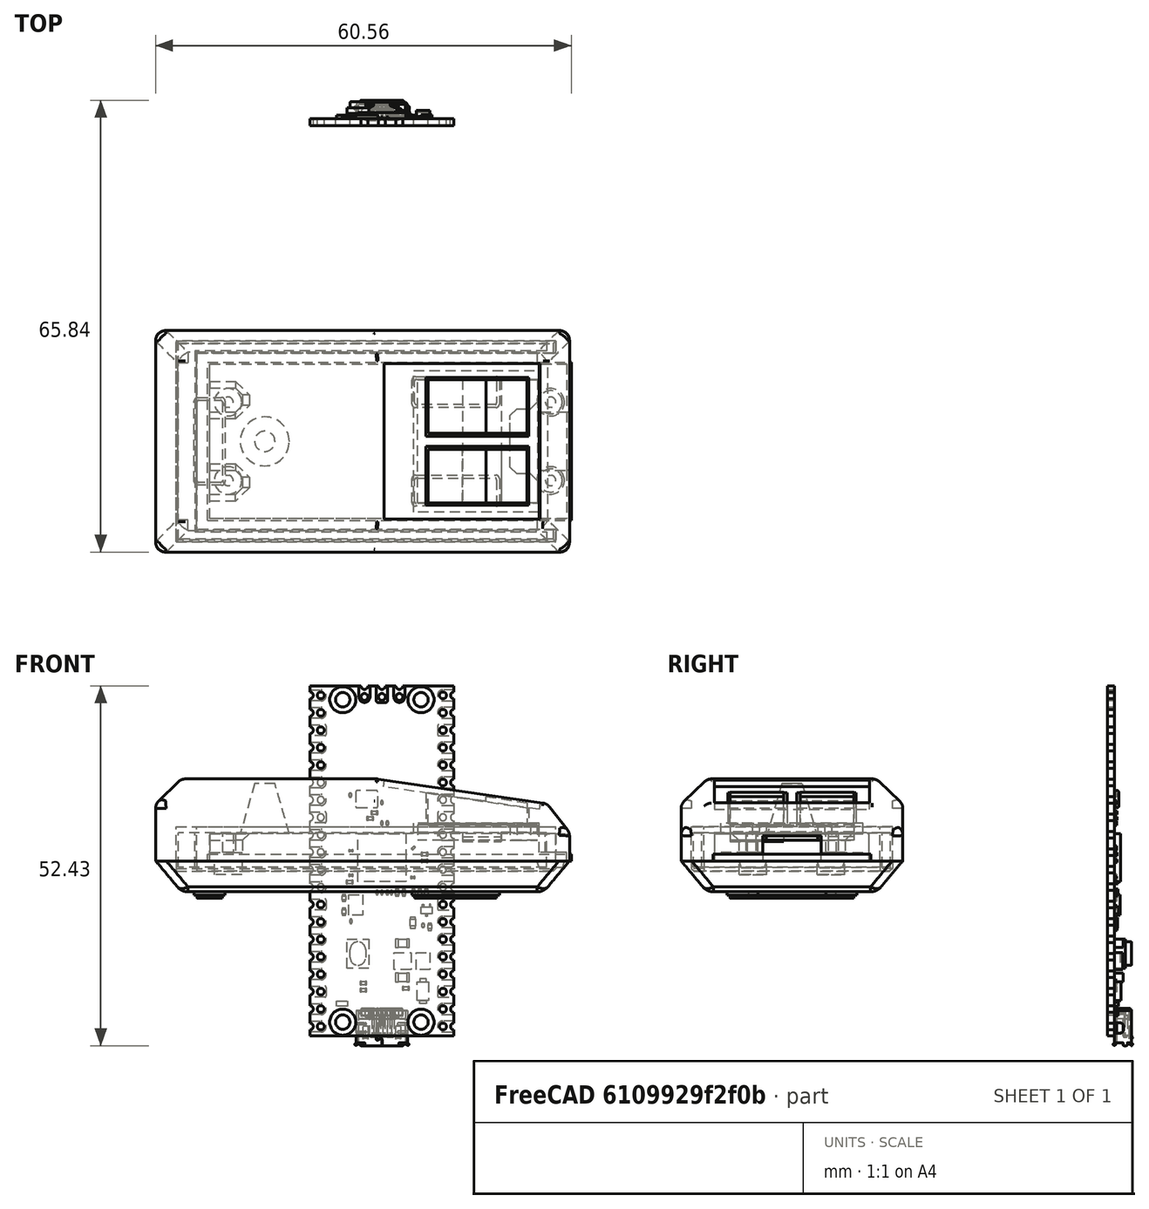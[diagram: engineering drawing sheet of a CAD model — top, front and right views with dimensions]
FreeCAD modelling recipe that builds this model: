
FCSTD DOCUMENT  (FreeCAD 0.22R36731 (Git))
Label: mouse
License: All rights reserved
LicenseURL: http://en.wikipedia.org/wiki/All_rights_reserved
objects: Part::Feature×116, App::Part×35, Sketcher::SketchObject×27, PartDesign::Pad×16, PartDesign::Pocket×16, PartDesign::Body×6, PartDesign::Chamfer×3, PartDesign::Fillet×2, Mesh::Feature×1, PartDesign::Plane×1, Part::Box×1
note: 225 computed .brp shape members not serialized (recipe doc carries the construction recipe); baked Part::Feature solids carry a one-line shape summary decoded from their .brp

FEATURE [Sketcher::SketchObject] Sketch
  AttachmentSupport = -> [XZ_Plane]
  FullyConstrained = true
  MapMode = 5
  Placement = pos=(0,0,0) rot=(1,0,0;1.5708rad)
  sketch-geometry (14):
    g0: LineSegment StartX=21.1514 StartY=8.48067 StartZ=0 EndX=15.1514 EndY=9.36067 EndZ=0
    g1: LineSegment StartX=15.1514 StartY=9.36067 StartZ=0 EndX=15.1514 EndY=8.76067 EndZ=0
    g2: LineSegment StartX=15.1514 StartY=8.76067 StartZ=0 EndX=6.70138 EndY=10 EndZ=0
    g3: LineSegment StartX=6.70138 StartY=10 StartZ=0 EndX=6.70138 EndY=5.25 EndZ=0
    g4: LineSegment StartX=6.70138 StartY=5.25 StartZ=0 EndX=5.20138 EndY=5.25 EndZ=0
    g5: LineSegment StartX=5.20138 StartY=5.25 StartZ=0 EndX=5.20138 EndY=4.25 EndZ=0
    g6: LineSegment StartX=5.20138 StartY=4.25 StartZ=0 EndX=11.74 EndY=4.25 EndZ=0
    g7: LineSegment StartX=11.74 StartY=4.25 StartZ=0 EndX=11.74 EndY=3 EndZ=0
    g8: LineSegment StartX=11.74 StartY=3 StartZ=0 EndX=17.37 EndY=3 EndZ=0
    g9: LineSegment StartX=17.37 StartY=3 StartZ=0 EndX=17.37 EndY=4.25 EndZ=0
    g10: LineSegment StartX=17.37 StartY=4.25 StartZ=0 EndX=22.6514 EndY=4.25 EndZ=0
    g11: LineSegment StartX=22.6514 StartY=4.25 StartZ=0 EndX=22.6514 EndY=5.25 EndZ=0
    g12: LineSegment StartX=22.6514 StartY=5.25 StartZ=0 EndX=21.1514 EndY=5.25 EndZ=0
    g13: LineSegment StartX=21.1514 StartY=5.25 StartZ=0 EndX=21.1514 EndY=8.48067 EndZ=0
  constraints (42):
    c: Coincident(g0,g1)
    c: Vertical(g1)
    c: Coincident(g1,g2)
    c: Coincident(g2,g3)
    c: Vertical(g3)
    c: Coincident(g3,g4)
    c: Coincident(g4,g5)
    c: Vertical(g5)
    c: Coincident(g5,g6)
    c: Horizontal(g6)
    c: Coincident(g6,g7)
    c: Coincident(g7,g8)
    c: Horizontal(g8)
    c: Coincident(g8,g9)
    c: Coincident(g9,g10)
    c: Coincident(g10,g11)
    c: Vertical(g11)
    c: Coincident(g11,g12)
    c: Coincident(g12,g13)
    c: Coincident(g13,g0)
    c: Vertical(g13)
    c: Parallel(g0,g2)
    c: DistanceX(g0) = 21.1514
    c: DistanceX(g0,g0) = 6
    c: DistanceX(g2,g2) = 8.45
    c: DistanceY(g0,g0) = 0.88
    c: DistanceY(g1,g1) = 0.6
    c: Vertical(g9)
    c: Vertical(g7)
    c: Horizontal(g10)
    c: Equal(g7,g9)
    c: DistanceX(g7) = 11.74
    c: DistanceX(g8,g8) = 5.63
    c: DistanceX(g4,g3) = 1.5
    c: DistanceY(g7) = 3
    c: Horizontal(g12)
    c: DistanceX(g12,g12) = 1.5
    c: Horizontal(g4)
    c: PointOnObject(g3,g12)
    c: DistanceY(g5,g5) = 1
    c: DistanceY(g7,g7) = 1.25
    c: DistanceY(g3,g3) = 4.75
FEATURE [PartDesign::Pad] Pad
  Direction = (0,-1,2e-16)
  Length = 18
  Length2 = 10
  Placement = pos=(0,0,0) rot=(1,0,0;1.5708rad)
  Profile = -> Sketch
  ReferenceAxis = -> Sketch [N_Axis]
  Refine = true
  Suppressed = false
  Type = 0
FEATURE [Mesh::Feature] mouse_bottom
FEATURE [Part::Feature] Part__Feature  label="PCB, Raspberry Pi Pico-R3"
  shape: bbox 21 x 1 x 51 mm, 416 faces (baked)
FEATURE [Part::Feature] Part__Feature001  label="MicroUSB Port, Raspberry Pi Pico-R3"
  Placement = pos=(0,0.5,-24.35) rot=(0,1,0;3.14159rad)
  shape: bbox 7.999 x 2.949 x 5.461 mm, 809 faces (baked)
FEATURE [Part::Feature] Part__Feature002  label="MicroUSB Port, Raspberry Pi Pico-R004"
  Placement = pos=(0,0.5,-24.35) rot=(0,1,0;3.14159rad)
  shape: bbox 6.982 x 2.155 x 3.937 mm, 206 faces (baked)
FEATURE [Part::Feature] Part__Feature003  label="MicroUSB Port, Raspberry Pi Pico-R005"
  Placement = pos=(0,0.5,-24.35) rot=(0,1,0;3.14159rad)
  shape: bbox 0.37 x 1.716 x 4 mm, 43 faces (baked)
FEATURE [Part::Feature] Part__Feature004  label="MicroUSB Port, Raspberry Pi Pico-R006"
  Placement = pos=(0,0.5,-24.35) rot=(0,1,0;3.14159rad)
  shape: bbox 0.37 x 1.716 x 4 mm, 43 faces (baked)
FEATURE [Part::Feature] Part__Feature005  label="MicroUSB Port, Raspberry Pi Pico-R007"
  Placement = pos=(0,0.5,-24.35) rot=(0,1,0;3.14159rad)
  shape: bbox 0.37 x 1.716 x 4 mm, 43 faces (baked)
FEATURE [Part::Feature] Part__Feature006  label="MicroUSB Port, Raspberry Pi Pico-R008"
  Placement = pos=(0,0.5,-24.35) rot=(0,1,0;3.14159rad)
  shape: bbox 0.37 x 1.716 x 4 mm, 43 faces (baked)
FEATURE [Part::Feature] Part__Feature007  label="MicroUSB Port, Raspberry Pi Pico-R009"
  Placement = pos=(0,0.5,-24.35) rot=(0,1,0;3.14159rad)
  shape: bbox 0.37 x 1.716 x 4 mm, 43 faces (baked)
FEATURE [App::Part] MicroUSB_Port__Raspberry_Pi_Pico_R3  label="MicroUSB Port, Raspberry Pi Pico-R010"
  Group = -> [Part__Feature001,Part__Feature002,Part__Feature003,Part__Feature004,Part__Feature005,Part__Feature006,Part__Feature007]
  Origin = -> Origin001
FEATURE [Part::Feature] Part__Feature008  label="RP2040 Microcontroller, Raspberry Pi Pico-R3"
  Placement = pos=(0,0.5,0.5) rot=(0,0,1;0rad)
  shape: bbox 7 x 0.9 x 7 mm, 6 faces (baked)
FEATURE [Part::Feature] Part__Feature009  label="SW1, Tact Switch, Raspberry Pi Pico-R3"
  Placement = pos=(-3.5,0.5,-13.5) rot=(0,0,1;0rad)
  shape: bbox 3.2 x 2.5 x 4.25 mm, 17 faces (baked)
FEATURE [Part::Feature] Part__Feature010  label="D1, Diode, Schottky, Raspberry Pi Pico-R3"
  Placement = pos=(6,0.5,-19) rot=(0,0,1;0rad)
  shape: bbox 1.65 x 0.95 x 3.6 mm, 14 faces (baked)
FEATURE [Part::Feature] Part__Feature011  label="D2, QSME-C194, LED, Raspberry Pi Pico-R3"
  Placement = pos=(-5.8,0.5,-20.8) rot=(0,0,1;0rad)
  shape: bbox 1.6 x 0.55 x 0.8 mm, 6 faces (baked)
FEATURE [Part::Feature] Part__Feature012  label="L1, Inductor, Raspberry Pi Pico-R3"
  Placement = pos=(6,0.5,-14.6) rot=(0,0,1;0rad)
  shape: bbox 2 x 1.2 x 2.5 mm, 6 faces (baked)
FEATURE [Part::Feature] Part__Feature013  label="U2, RT6150B-33GQW, Buck Boost Converter, Raspberry Pi Pico-R3"
  Placement = pos=(3,0.5,-14.6) rot=(0,0,1;0rad)
  shape: bbox 2.5 x 0.8 x 2.5 mm, 6 faces (baked)
FEATURE [Part::Feature] Part__Feature014  label="U3, W25Q16JVUXIQ, Serial NOR Flash 16 Mbit, Raspberry Pi Pico-R3"
  Placement = pos=(-3.8,0.5,-6.4) rot=(0,0,1;0rad)
  shape: bbox 2 x 0.8 x 3 mm, 6 faces (baked)
FEATURE [Part::Feature] Part__Feature015  label="Q1, MOSFET, DMG1012T, Raspberry Pi Pico-R3"
  Placement = pos=(6.5,0.5,-7.2) rot=(0,0,1;0rad)
  shape: bbox 1.6 x 0.6 x 1.8 mm, 18 faces (baked)
FEATURE [Part::Feature] Part__Feature016  label="X1, X12M000000S096, 12 Mhz Crystal Resonator, Raspberry Pi Pico-R3"
  Placement = pos=(-2.2,0.5,9) rot=(0,0,1;0rad)
  shape: bbox 3.2 x 0.6 x 2.5 mm, 18 faces (baked)
FEATURE [Part::Feature] Part__Feature017  label="SMD Resistor, Configurable, Raspberry Pi Pico-R3_R1"
  Placement = pos=(6.2,0.5,1) rot=(0,1,0;1.5708rad)
  shape: bbox 0.6 x 0.35 x 0.5 mm, 6 faces (baked)
FEATURE [Part::Feature] Part__Feature018  label="SMD Resistor, Configurable, Raspberry Pi Pico-R3_R002"
  Placement = pos=(6.2,0.5,1) rot=(0,1,0;1.5708rad)
  shape: bbox 0.2 x 0.35 x 0.5 mm, 6 faces (baked)
FEATURE [Part::Feature] Part__Feature019  label="SMD Resistor, Configurable, Raspberry Pi Pico-R3_R003"
  Placement = pos=(6.2,0.5,1) rot=(0,1,0;1.5708rad)
  shape: bbox 0.2 x 0.35 x 0.5 mm, 6 faces (baked)
FEATURE [App::Part] SMD_Resistor__Configurable__Raspberry_Pi_Pico_R3_R1  label="SMD Resistor, Configurable, Raspberry Pi Pico-R3_R004"
  Group = -> [Part__Feature017,Part__Feature018,Part__Feature019]
  Origin = -> Origin002
FEATURE [Part::Feature] Part__Feature020  label="SMD Resistor, Configurable, Raspberry Pi Pico-R3_R2"
  Placement = pos=(3.5,0.5,-18.6) rot=(0,1,0;1.5708rad)
  shape: bbox 0.6 x 0.35 x 0.5 mm, 6 faces (baked)
FEATURE [Part::Feature] Part__Feature021  label="SMD Resistor, Configurable, Raspberry Pi Pico-R3_R005"
  Placement = pos=(3.5,0.5,-18.6) rot=(0,1,0;1.5708rad)
  shape: bbox 0.2 x 0.35 x 0.5 mm, 6 faces (baked)
FEATURE [Part::Feature] Part__Feature022  label="SMD Resistor, Configurable, Raspberry Pi Pico-R3_R006"
  Placement = pos=(3.5,0.5,-18.6) rot=(0,1,0;1.5708rad)
  shape: bbox 0.2 x 0.35 x 0.5 mm, 6 faces (baked)
FEATURE [App::Part] SMD_Resistor__Configurable__Raspberry_Pi_Pico_R3_R2  label="SMD Resistor, Configurable, Raspberry Pi Pico-R3_R007"
  Group = -> [Part__Feature020,Part__Feature021,Part__Feature022]
  Origin = -> Origin003
FEATURE [Part::Feature] Part__Feature023  label="SMD Resistor, Configurable, Raspberry Pi Pico-R3_R3"
  Placement = pos=(-2.7,0.5,-17.8) rot=(0,1,0;1.5708rad)
  shape: bbox 0.6 x 0.35 x 0.5 mm, 6 faces (baked)
FEATURE [Part::Feature] Part__Feature024  label="SMD Resistor, Configurable, Raspberry Pi Pico-R3_R008"
  Placement = pos=(-2.7,0.5,-17.8) rot=(0,1,0;1.5708rad)
  shape: bbox 0.2 x 0.35 x 0.5 mm, 6 faces (baked)
FEATURE [Part::Feature] Part__Feature025  label="SMD Resistor, Configurable, Raspberry Pi Pico-R3_R009"
  Placement = pos=(-2.7,0.5,-17.8) rot=(0,1,0;1.5708rad)
  shape: bbox 0.2 x 0.35 x 0.5 mm, 6 faces (baked)
FEATURE [App::Part] SMD_Resistor__Configurable__Raspberry_Pi_Pico_R3_R3  label="SMD Resistor, Configurable, Raspberry Pi Pico-R3_R010"
  Group = -> [Part__Feature023,Part__Feature024,Part__Feature025]
  Origin = -> Origin004
FEATURE [Part::Feature] Part__Feature026  label="SMD Resistor, Configurable, Raspberry Pi Pico-R3_R4"
  Placement = pos=(-5.5,0.5,-5.4) rot=(0,1,0;3.14159rad)
  shape: bbox 0.5 x 0.35 x 0.6 mm, 6 faces (baked)
FEATURE [Part::Feature] Part__Feature027  label="SMD Resistor, Configurable, Raspberry Pi Pico-R3_R011"
  Placement = pos=(-5.5,0.5,-5.4) rot=(0,1,0;3.14159rad)
  shape: bbox 0.5 x 0.35 x 0.2 mm, 6 faces (baked)
FEATURE [Part::Feature] Part__Feature028  label="SMD Resistor, Configurable, Raspberry Pi Pico-R3_R012"
  Placement = pos=(-5.5,0.5,-5.4) rot=(0,1,0;3.14159rad)
  shape: bbox 0.5 x 0.35 x 0.2 mm, 6 faces (baked)
FEATURE [App::Part] SMD_Resistor__Configurable__Raspberry_Pi_Pico_R3_R4  label="SMD Resistor, Configurable, Raspberry Pi Pico-R3_R013"
  Group = -> [Part__Feature026,Part__Feature027,Part__Feature028]
  Origin = -> Origin005
FEATURE [Part::Feature] Part__Feature029  label="SMD Resistor, Configurable, Raspberry Pi Pico-R3_R5"
  Placement = pos=(7,0.5,-9.6) rot=(0,1,0;3.14159rad)
  shape: bbox 0.5 x 0.35 x 0.6 mm, 6 faces (baked)
FEATURE [Part::Feature] Part__Feature030  label="SMD Resistor, Configurable, Raspberry Pi Pico-R3_R014"
  Placement = pos=(7,0.5,-9.6) rot=(0,1,0;3.14159rad)
  shape: bbox 0.5 x 0.35 x 0.2 mm, 6 faces (baked)
FEATURE [Part::Feature] Part__Feature031  label="SMD Resistor, Configurable, Raspberry Pi Pico-R3_R015"
  Placement = pos=(7,0.5,-9.6) rot=(0,1,0;3.14159rad)
  shape: bbox 0.5 x 0.35 x 0.2 mm, 6 faces (baked)
FEATURE [App::Part] SMD_Resistor__Configurable__Raspberry_Pi_Pico_R3_R5  label="SMD Resistor, Configurable, Raspberry Pi Pico-R3_R016"
  Group = -> [Part__Feature029,Part__Feature030,Part__Feature031]
  Origin = -> Origin006
FEATURE [Part::Feature] Part__Feature032  label="SMD Resistor, Configurable, Raspberry Pi Pico-R3_R6"
  Placement = pos=(6.5,0.5,-4.6) rot=(0,1,0;3.14159rad)
  shape: bbox 0.5 x 0.35 x 0.6 mm, 6 faces (baked)
FEATURE [Part::Feature] Part__Feature033  label="SMD Resistor, Configurable, Raspberry Pi Pico-R3_R017"
  Placement = pos=(6.5,0.5,-4.6) rot=(0,1,0;3.14159rad)
  shape: bbox 0.5 x 0.35 x 0.2 mm, 6 faces (baked)
FEATURE [Part::Feature] Part__Feature034  label="SMD Resistor, Configurable, Raspberry Pi Pico-R3_R018"
  Placement = pos=(6.5,0.5,-4.6) rot=(0,1,0;3.14159rad)
  shape: bbox 0.5 x 0.35 x 0.2 mm, 6 faces (baked)
FEATURE [App::Part] SMD_Resistor__Configurable__Raspberry_Pi_Pico_R3_R6  label="SMD Resistor, Configurable, Raspberry Pi Pico-R3_R019"
  Group = -> [Part__Feature032,Part__Feature033,Part__Feature034]
  Origin = -> Origin007
FEATURE [Part::Feature] Part__Feature035  label="SMD Resistor, Configurable, Raspberry Pi Pico-R3_R7"
  Placement = pos=(4.5,0.5,-9) rot=(0,1,0;3.14159rad)
  shape: bbox 0.8 x 0.45 x 1 mm, 6 faces (baked)
FEATURE [Part::Feature] Part__Feature036  label="SMD Resistor, Configurable, Raspberry Pi Pico-R3_R020"
  Placement = pos=(4.5,0.5,-9) rot=(0,1,0;3.14159rad)
  shape: bbox 0.8 x 0.45 x 0.3 mm, 6 faces (baked)
FEATURE [Part::Feature] Part__Feature037  label="SMD Resistor, Configurable, Raspberry Pi Pico-R3_R021"
  Placement = pos=(4.5,0.5,-9) rot=(0,1,0;3.14159rad)
  shape: bbox 0.8 x 0.45 x 0.3 mm, 6 faces (baked)
FEATURE [App::Part] SMD_Resistor__Configurable__Raspberry_Pi_Pico_R3_R7  label="SMD Resistor, Configurable, Raspberry Pi Pico-R3_R022"
  Group = -> [Part__Feature035,Part__Feature036,Part__Feature037]
  Origin = -> Origin008
FEATURE [Part::Feature] Part__Feature038  label="SMD Resistor, Configurable, Raspberry Pi Pico-R3_R8"
  Placement = pos=(-2.7,0.5,-18.8) rot=(0,1,0;1.5708rad)
  shape: bbox 0.6 x 0.35 x 0.5 mm, 6 faces (baked)
FEATURE [Part::Feature] Part__Feature039  label="SMD Resistor, Configurable, Raspberry Pi Pico-R3_R023"
  Placement = pos=(-2.7,0.5,-18.8) rot=(0,1,0;1.5708rad)
  shape: bbox 0.2 x 0.35 x 0.5 mm, 6 faces (baked)
FEATURE [Part::Feature] Part__Feature040  label="SMD Resistor, Configurable, Raspberry Pi Pico-R3_R024"
  Placement = pos=(-2.7,0.5,-18.8) rot=(0,1,0;1.5708rad)
  shape: bbox 0.2 x 0.35 x 0.5 mm, 6 faces (baked)
FEATURE [App::Part] SMD_Resistor__Configurable__Raspberry_Pi_Pico_R3_R8  label="SMD Resistor, Configurable, Raspberry Pi Pico-R3_R025"
  Group = -> [Part__Feature038,Part__Feature039,Part__Feature040]
  Origin = -> Origin009
FEATURE [Part::Feature] Part__Feature041  label="SMD Resistor, Configurable, Raspberry Pi Pico-R3_R9"
  Placement = pos=(5.5,0.5,-4.6) rot=(0,1,0;3.14159rad)
  shape: bbox 0.5 x 0.35 x 0.6 mm, 6 faces (baked)
FEATURE [Part::Feature] Part__Feature042  label="SMD Resistor, Configurable, Raspberry Pi Pico-R3_R026"
  Placement = pos=(5.5,0.5,-4.6) rot=(0,1,0;3.14159rad)
  shape: bbox 0.5 x 0.35 x 0.2 mm, 6 faces (baked)
FEATURE [Part::Feature] Part__Feature043  label="SMD Resistor, Configurable, Raspberry Pi Pico-R3_R027"
  Placement = pos=(5.5,0.5,-4.6) rot=(0,1,0;3.14159rad)
  shape: bbox 0.5 x 0.35 x 0.2 mm, 6 faces (baked)
FEATURE [App::Part] SMD_Resistor__Configurable__Raspberry_Pi_Pico_R3_R9  label="SMD Resistor, Configurable, Raspberry Pi Pico-R3_R028"
  Group = -> [Part__Feature041,Part__Feature042,Part__Feature043]
  Origin = -> Origin010
FEATURE [Part::Feature] Part__Feature044  label="SMD Resistor, Configurable, Raspberry Pi Pico-R3_R10"
  Placement = pos=(6.2,0.5,-1e-16) rot=(0,1,0;1.5708rad)
  shape: bbox 0.6 x 0.35 x 0.5 mm, 6 faces (baked)
FEATURE [Part::Feature] Part__Feature045  label="SMD Resistor, Configurable, Raspberry Pi Pico-R3_R029"
  Placement = pos=(6.2,0.5,-1e-16) rot=(0,1,0;1.5708rad)
  shape: bbox 0.2 x 0.35 x 0.5 mm, 6 faces (baked)
FEATURE [Part::Feature] Part__Feature046  label="SMD Resistor, Configurable, Raspberry Pi Pico-R3_R030"
  Placement = pos=(6.2,0.5,-1e-16) rot=(0,1,0;1.5708rad)
  shape: bbox 0.2 x 0.35 x 0.5 mm, 6 faces (baked)
FEATURE [App::Part] SMD_Resistor__Configurable__Raspberry_Pi_Pico_R3_R10  label="SMD Resistor, Configurable, Raspberry Pi Pico-R3_R031"
  Group = -> [Part__Feature044,Part__Feature045,Part__Feature046]
  Origin = -> Origin011
FEATURE [Part::Feature] Part__Feature047  label="SMD Resistor, Configurable, Raspberry Pi Pico-R3_R11"
  Placement = pos=(-5.5,0.5,-7.4) rot=(0,0,1;0rad)
  shape: bbox 0.5 x 0.35 x 0.6 mm, 6 faces (baked)
FEATURE [Part::Feature] Part__Feature048  label="SMD Resistor, Configurable, Raspberry Pi Pico-R3_R032"
  Placement = pos=(-5.5,0.5,-7.4) rot=(0,0,1;0rad)
  shape: bbox 0.5 x 0.35 x 0.2 mm, 6 faces (baked)
FEATURE [Part::Feature] Part__Feature049  label="SMD Resistor, Configurable, Raspberry Pi Pico-R3_R033"
  Placement = pos=(-5.5,0.5,-7.4) rot=(0,0,1;0rad)
  shape: bbox 0.5 x 0.35 x 0.2 mm, 6 faces (baked)
FEATURE [App::Part] SMD_Resistor__Configurable__Raspberry_Pi_Pico_R3_R11  label="SMD Resistor, Configurable, Raspberry Pi Pico-R3_R034"
  Group = -> [Part__Feature047,Part__Feature048,Part__Feature049]
  Origin = -> Origin012
FEATURE [Part::Feature] Part__Feature050  label="SMD Resistor, Configurable, Raspberry Pi Pico-R3_R12"
  Placement = pos=(0.8,0.5,-4.6) rot=(0,1,0;3.14159rad)
  shape: bbox 0.3 x 0.23 x 0.4 mm, 6 faces (baked)
FEATURE [Part::Feature] Part__Feature051  label="SMD Resistor, Configurable, Raspberry Pi Pico-R3_R035"
  Placement = pos=(0.8,0.5,-4.6) rot=(0,1,0;3.14159rad)
  shape: bbox 0.3 x 0.23 x 0.1 mm, 6 faces (baked)
FEATURE [Part::Feature] Part__Feature052  label="SMD Resistor, Configurable, Raspberry Pi Pico-R3_R036"
  Placement = pos=(0.8,0.5,-4.6) rot=(0,1,0;3.14159rad)
  shape: bbox 0.3 x 0.23 x 0.1 mm, 6 faces (baked)
FEATURE [App::Part] SMD_Resistor__Configurable__Raspberry_Pi_Pico_R3_R12  label="SMD Resistor, Configurable, Raspberry Pi Pico-R3_R037"
  Group = -> [Part__Feature050,Part__Feature051,Part__Feature052]
  Origin = -> Origin013
FEATURE [Part::Feature] Part__Feature053  label="SMD Resistor, Configurable, Raspberry Pi Pico-R3_R13"
  Placement = pos=(1.4,0.5,-4.6) rot=(0,1,0;3.14159rad)
  shape: bbox 0.3 x 0.23 x 0.4 mm, 6 faces (baked)
FEATURE [Part::Feature] Part__Feature054  label="SMD Resistor, Configurable, Raspberry Pi Pico-R3_R038"
  Placement = pos=(1.4,0.5,-4.6) rot=(0,1,0;3.14159rad)
  shape: bbox 0.3 x 0.23 x 0.1 mm, 6 faces (baked)
FEATURE [Part::Feature] Part__Feature055  label="SMD Resistor, Configurable, Raspberry Pi Pico-R3_R039"
  Placement = pos=(1.4,0.5,-4.6) rot=(0,1,0;3.14159rad)
  shape: bbox 0.3 x 0.23 x 0.1 mm, 6 faces (baked)
FEATURE [App::Part] SMD_Resistor__Configurable__Raspberry_Pi_Pico_R3_R13  label="SMD Resistor, Configurable, Raspberry Pi Pico-R3_R040"
  Group = -> [Part__Feature053,Part__Feature054,Part__Feature055]
  Origin = -> Origin014
FEATURE [Part::Feature] Part__Feature056  label="SMD Resistor, Configurable, Raspberry Pi Pico-R3_R14"
  Placement = pos=(-1.1,0.5,7) rot=(0,1,0;1.5708rad)
  shape: bbox 0.6 x 0.35 x 0.5 mm, 6 faces (baked)
FEATURE [Part::Feature] Part__Feature057  label="SMD Resistor, Configurable, Raspberry Pi Pico-R3_R041"
  Placement = pos=(-1.1,0.5,7) rot=(0,1,0;1.5708rad)
  shape: bbox 0.2 x 0.35 x 0.5 mm, 6 faces (baked)
FEATURE [Part::Feature] Part__Feature058  label="SMD Resistor, Configurable, Raspberry Pi Pico-R3_R042"
  Placement = pos=(-1.1,0.5,7) rot=(0,1,0;1.5708rad)
  shape: bbox 0.2 x 0.35 x 0.5 mm, 6 faces (baked)
FEATURE [App::Part] SMD_Resistor__Configurable__Raspberry_Pi_Pico_R3_R14  label="SMD Resistor, Configurable, Raspberry Pi Pico-R3_R043"
  Group = -> [Part__Feature056,Part__Feature057,Part__Feature058]
  Origin = -> Origin015
FEATURE [Part::Feature] Part__Feature059  label="SMD Resistor, Configurable, Raspberry Pi Pico-R3_R15"
  Placement = pos=(-1.7,0.5,6.2) rot=(0,1,0;1.5708rad)
  shape: bbox 0.6 x 0.35 x 0.5 mm, 6 faces (baked)
FEATURE [Part::Feature] Part__Feature060  label="SMD Resistor, Configurable, Raspberry Pi Pico-R3_R044"
  Placement = pos=(-1.7,0.5,6.2) rot=(0,1,0;1.5708rad)
  shape: bbox 0.2 x 0.35 x 0.5 mm, 6 faces (baked)
FEATURE [Part::Feature] Part__Feature061  label="SMD Resistor, Configurable, Raspberry Pi Pico-R3_R045"
  Placement = pos=(-1.7,0.5,6.2) rot=(0,1,0;1.5708rad)
  shape: bbox 0.2 x 0.35 x 0.5 mm, 6 faces (baked)
FEATURE [App::Part] SMD_Resistor__Configurable__Raspberry_Pi_Pico_R3_R15  label="SMD Resistor, Configurable, Raspberry Pi Pico-R3_R046"
  Group = -> [Part__Feature059,Part__Feature060,Part__Feature061]
  Origin = -> Origin016
FEATURE [Part::Feature] Part__Feature062  label="SMD Capacitor, Configurable, Raspberry Pi Pico-R3_C1"
  Placement = pos=(3,0.5,-17) rot=(0,1,0;1.5708rad)
  shape: bbox 1.2 x 1.25 x 1.25 mm, 6 faces (baked)
FEATURE [Part::Feature] Part__Feature063  label="SMD Capacitor, Configurable, Raspberry Pi Pico-R3_C002"
  Placement = pos=(3,0.5,-17) rot=(0,1,0;1.5708rad)
  shape: bbox 0.4 x 1.25 x 1.25 mm, 6 faces (baked)
FEATURE [Part::Feature] Part__Feature064  label="SMD Capacitor, Configurable, Raspberry Pi Pico-R3_C003"
  Placement = pos=(3,0.5,-17) rot=(0,1,0;1.5708rad)
  shape: bbox 0.4 x 1.25 x 1.25 mm, 6 faces (baked)
FEATURE [App::Part] SMD_Capacitor__Configurable__Raspberry_Pi_Pico_R3_C1  label="SMD Capacitor, Configurable, Raspberry Pi Pico-R3_C004"
  Group = -> [Part__Feature062,Part__Feature063,Part__Feature064]
  Origin = -> Origin017
FEATURE [Part::Feature] Part__Feature065  label="SMD Capacitor, Configurable, Raspberry Pi Pico-R3_C2"
  Placement = pos=(3,0.5,-12) rot=(0,1,0;1.5708rad)
  shape: bbox 1.2 x 1.25 x 1.25 mm, 6 faces (baked)
FEATURE [Part::Feature] Part__Feature066  label="SMD Capacitor, Configurable, Raspberry Pi Pico-R3_C005"
  Placement = pos=(3,0.5,-12) rot=(0,1,0;1.5708rad)
  shape: bbox 0.4 x 1.25 x 1.25 mm, 6 faces (baked)
FEATURE [Part::Feature] Part__Feature067  label="SMD Capacitor, Configurable, Raspberry Pi Pico-R3_C006"
  Placement = pos=(3,0.5,-12) rot=(0,1,0;1.5708rad)
  shape: bbox 0.4 x 1.25 x 1.25 mm, 6 faces (baked)
FEATURE [App::Part] SMD_Capacitor__Configurable__Raspberry_Pi_Pico_R3_C2  label="SMD Capacitor, Configurable, Raspberry Pi Pico-R3_C007"
  Group = -> [Part__Feature065,Part__Feature066,Part__Feature067]
  Origin = -> Origin018
FEATURE [Part::Feature] Part__Feature068  label="SMD Capacitor, Configurable, Raspberry Pi Pico-R3_C3"
  Placement = pos=(6,0.5,-9.4) rot=(0,0,1;0rad)
  shape: bbox 0.3 x 0.3 x 0.4 mm, 6 faces (baked)
FEATURE [Part::Feature] Part__Feature069  label="SMD Capacitor, Configurable, Raspberry Pi Pico-R3_C008"
  Placement = pos=(6,0.5,-9.4) rot=(0,0,1;0rad)
  shape: bbox 0.3 x 0.3 x 0.1 mm, 6 faces (baked)
FEATURE [Part::Feature] Part__Feature070  label="SMD Capacitor, Configurable, Raspberry Pi Pico-R3_C009"
  Placement = pos=(6,0.5,-9.4) rot=(0,0,1;0rad)
  shape: bbox 0.3 x 0.3 x 0.1 mm, 6 faces (baked)
FEATURE [App::Part] SMD_Capacitor__Configurable__Raspberry_Pi_Pico_R3_C3  label="SMD Capacitor, Configurable, Raspberry Pi Pico-R3_C010"
  Group = -> [Part__Feature068,Part__Feature069,Part__Feature070]
  Origin = -> Origin019
FEATURE [Part::Feature] Part__Feature071  label="SMD Capacitor, Configurable, Raspberry Pi Pico-R3_C4"
  Placement = pos=(-4.5,0.5,-2.1) rot=(0,-1,0;1.5708rad)
  shape: bbox 0.4 x 0.3 x 0.3 mm, 6 faces (baked)
FEATURE [Part::Feature] Part__Feature072  label="SMD Capacitor, Configurable, Raspberry Pi Pico-R3_C011"
  Placement = pos=(-4.5,0.5,-2.1) rot=(0,-1,0;1.5708rad)
  shape: bbox 0.1 x 0.3 x 0.3 mm, 6 faces (baked)
FEATURE [Part::Feature] Part__Feature073  label="SMD Capacitor, Configurable, Raspberry Pi Pico-R3_C012"
  Placement = pos=(-4.5,0.5,-2.1) rot=(0,-1,0;1.5708rad)
  shape: bbox 0.1 x 0.3 x 0.3 mm, 6 faces (baked)
FEATURE [App::Part] SMD_Capacitor__Configurable__Raspberry_Pi_Pico_R3_C4  label="SMD Capacitor, Configurable, Raspberry Pi Pico-R3_C013"
  Group = -> [Part__Feature071,Part__Feature072,Part__Feature073]
  Origin = -> Origin020
FEATURE [Part::Feature] Part__Feature074  label="SMD Capacitor, Configurable, Raspberry Pi Pico-R3_C5"
  Placement = pos=(-4.5,0.5,1.5) rot=(0,-1,0;1.5708rad)
  shape: bbox 0.4 x 0.3 x 0.3 mm, 6 faces (baked)
FEATURE [Part::Feature] Part__Feature075  label="SMD Capacitor, Configurable, Raspberry Pi Pico-R3_C014"
  Placement = pos=(-4.5,0.5,1.5) rot=(0,-1,0;1.5708rad)
  shape: bbox 0.1 x 0.3 x 0.3 mm, 6 faces (baked)
FEATURE [Part::Feature] Part__Feature076  label="SMD Capacitor, Configurable, Raspberry Pi Pico-R3_C015"
  Placement = pos=(-4.5,0.5,1.5) rot=(0,-1,0;1.5708rad)
  shape: bbox 0.1 x 0.3 x 0.3 mm, 6 faces (baked)
FEATURE [App::Part] SMD_Capacitor__Configurable__Raspberry_Pi_Pico_R3_C5  label="SMD Capacitor, Configurable, Raspberry Pi Pico-R3_C016"
  Group = -> [Part__Feature074,Part__Feature075,Part__Feature076]
  Origin = -> Origin021
FEATURE [Part::Feature] Part__Feature077  label="SMD Capacitor, Configurable, Raspberry Pi Pico-R3_C6"
  Placement = pos=(4.6,0.5,1.9) rot=(0,1,0;0.785398rad)
  shape: bbox 0.495 x 0.3 x 0.495 mm, 6 faces (baked)
FEATURE [Part::Feature] Part__Feature078  label="SMD Capacitor, Configurable, Raspberry Pi Pico-R3_C017"
  Placement = pos=(4.6,0.5,1.9) rot=(0,1,0;0.785398rad)
  shape: bbox 0.2828 x 0.3 x 0.2828 mm, 6 faces (baked)
FEATURE [Part::Feature] Part__Feature079  label="SMD Capacitor, Configurable, Raspberry Pi Pico-R3_C018"
  Placement = pos=(4.6,0.5,1.9) rot=(0,1,0;0.785398rad)
  shape: bbox 0.2828 x 0.3 x 0.2828 mm, 6 faces (baked)
FEATURE [App::Part] SMD_Capacitor__Configurable__Raspberry_Pi_Pico_R3_C6  label="SMD Capacitor, Configurable, Raspberry Pi Pico-R3_C019"
  Group = -> [Part__Feature077,Part__Feature078,Part__Feature079]
  Origin = -> Origin022
FEATURE [Part::Feature] Part__Feature080  label="SMD Capacitor, Configurable, Raspberry Pi Pico-R3_C7"
  Placement = pos=(4.5,0.5,-2.4) rot=(0,-1,0;1.5708rad)
  shape: bbox 0.4 x 0.3 x 0.3 mm, 6 faces (baked)
FEATURE [Part::Feature] Part__Feature081  label="SMD Capacitor, Configurable, Raspberry Pi Pico-R3_C020"
  Placement = pos=(4.5,0.5,-2.4) rot=(0,-1,0;1.5708rad)
  shape: bbox 0.1 x 0.3 x 0.3 mm, 6 faces (baked)
FEATURE [Part::Feature] Part__Feature082  label="SMD Capacitor, Configurable, Raspberry Pi Pico-R3_C021"
  Placement = pos=(4.5,0.5,-2.4) rot=(0,-1,0;1.5708rad)
  shape: bbox 0.1 x 0.3 x 0.3 mm, 6 faces (baked)
FEATURE [App::Part] SMD_Capacitor__Configurable__Raspberry_Pi_Pico_R3_C7  label="SMD Capacitor, Configurable, Raspberry Pi Pico-R3_C022"
  Group = -> [Part__Feature080,Part__Feature081,Part__Feature082]
  Origin = -> Origin023
FEATURE [Part::Feature] Part__Feature083  label="SMD Capacitor, Configurable, Raspberry Pi Pico-R3_C8"
  Placement = pos=(0,0.5,5.5) rot=(0,0,1;0rad)
  shape: bbox 0.3 x 0.3 x 0.4 mm, 6 faces (baked)
FEATURE [Part::Feature] Part__Feature084  label="SMD Capacitor, Configurable, Raspberry Pi Pico-R3_C023"
  Placement = pos=(0,0.5,5.5) rot=(0,0,1;0rad)
  shape: bbox 0.3 x 0.3 x 0.1 mm, 6 faces (baked)
FEATURE [Part::Feature] Part__Feature085  label="SMD Capacitor, Configurable, Raspberry Pi Pico-R3_C024"
  Placement = pos=(0,0.5,5.5) rot=(0,0,1;0rad)
  shape: bbox 0.3 x 0.3 x 0.1 mm, 6 faces (baked)
FEATURE [App::Part] SMD_Capacitor__Configurable__Raspberry_Pi_Pico_R3_C8  label="SMD Capacitor, Configurable, Raspberry Pi Pico-R3_C025"
  Group = -> [Part__Feature083,Part__Feature084,Part__Feature085]
  Origin = -> Origin024
FEATURE [Part::Feature] Part__Feature086  label="SMD Capacitor, Configurable, Raspberry Pi Pico-R3_C9"
  Placement = pos=(0.8,0.5,5.5) rot=(0,0,1;0rad)
  shape: bbox 0.3 x 0.3 x 0.4 mm, 6 faces (baked)
FEATURE [Part::Feature] Part__Feature087  label="SMD Capacitor, Configurable, Raspberry Pi Pico-R3_C026"
  Placement = pos=(0.8,0.5,5.5) rot=(0,0,1;0rad)
  shape: bbox 0.3 x 0.3 x 0.1 mm, 6 faces (baked)
FEATURE [Part::Feature] Part__Feature088  label="SMD Capacitor, Configurable, Raspberry Pi Pico-R3_C027"
  Placement = pos=(0.8,0.5,5.5) rot=(0,0,1;0rad)
  shape: bbox 0.3 x 0.3 x 0.1 mm, 6 faces (baked)
FEATURE [App::Part] SMD_Capacitor__Configurable__Raspberry_Pi_Pico_R3_C9  label="SMD Capacitor, Configurable, Raspberry Pi Pico-R3_C028"
  Group = -> [Part__Feature086,Part__Feature087,Part__Feature088]
  Origin = -> Origin025
FEATURE [Part::Feature] Part__Feature089  label="SMD Capacitor, Configurable, Raspberry Pi Pico-R3_C10"
  Placement = pos=(0,0.5,-4.6) rot=(0,0,1;0rad)
  shape: bbox 0.3 x 0.3 x 0.4 mm, 6 faces (baked)
FEATURE [Part::Feature] Part__Feature090  label="SMD Capacitor, Configurable, Raspberry Pi Pico-R3_C029"
  Placement = pos=(0,0.5,-4.6) rot=(0,0,1;0rad)
  shape: bbox 0.3 x 0.3 x 0.1 mm, 6 faces (baked)
FEATURE [Part::Feature] Part__Feature091  label="SMD Capacitor, Configurable, Raspberry Pi Pico-R3_C030"
  Placement = pos=(0,0.5,-4.6) rot=(0,0,1;0rad)
  shape: bbox 0.3 x 0.3 x 0.1 mm, 6 faces (baked)
FEATURE [App::Part] SMD_Capacitor__Configurable__Raspberry_Pi_Pico_R3_C10  label="SMD Capacitor, Configurable, Raspberry Pi Pico-R3_C031"
  Group = -> [Part__Feature089,Part__Feature090,Part__Feature091]
  Origin = -> Origin026
FEATURE [Part::Feature] Part__Feature092  label="SMD Capacitor, Configurable, Raspberry Pi Pico-R3_C11"
  Placement = pos=(-0.7,0.5,-4.6) rot=(0,0,1;0rad)
  shape: bbox 0.3 x 0.3 x 0.4 mm, 6 faces (baked)
FEATURE [Part::Feature] Part__Feature093  label="SMD Capacitor, Configurable, Raspberry Pi Pico-R3_C032"
  Placement = pos=(-0.7,0.5,-4.6) rot=(0,0,1;0rad)
  shape: bbox 0.3 x 0.3 x 0.1 mm, 6 faces (baked)
FEATURE [Part::Feature] Part__Feature094  label="SMD Capacitor, Configurable, Raspberry Pi Pico-R3_C033"
  Placement = pos=(-0.7,0.5,-4.6) rot=(0,0,1;0rad)
  shape: bbox 0.3 x 0.3 x 0.1 mm, 6 faces (baked)
FEATURE [App::Part] SMD_Capacitor__Configurable__Raspberry_Pi_Pico_R3_C11  label="SMD Capacitor, Configurable, Raspberry Pi Pico-R3_C034"
  Group = -> [Part__Feature092,Part__Feature093,Part__Feature094]
  Origin = -> Origin027
FEATURE [Part::Feature] Part__Feature095  label="SMD Capacitor, Configurable, Raspberry Pi Pico-R3_C12"
  Placement = pos=(2.2,0.5,-4.6) rot=(0,0,1;0rad)
  shape: bbox 0.5 x 0.5 x 0.6 mm, 6 faces (baked)
FEATURE [Part::Feature] Part__Feature096  label="SMD Capacitor, Configurable, Raspberry Pi Pico-R3_C035"
  Placement = pos=(2.2,0.5,-4.6) rot=(0,0,1;0rad)
  shape: bbox 0.5 x 0.5 x 0.2 mm, 6 faces (baked)
FEATURE [Part::Feature] Part__Feature097  label="SMD Capacitor, Configurable, Raspberry Pi Pico-R3_C036"
  Placement = pos=(2.2,0.5,-4.6) rot=(0,0,1;0rad)
  shape: bbox 0.5 x 0.5 x 0.2 mm, 6 faces (baked)
FEATURE [App::Part] SMD_Capacitor__Configurable__Raspberry_Pi_Pico_R3_C12  label="SMD Capacitor, Configurable, Raspberry Pi Pico-R3_C037"
  Group = -> [Part__Feature095,Part__Feature096,Part__Feature097]
  Origin = -> Origin028
FEATURE [Part::Feature] Part__Feature098  label="SMD Capacitor, Configurable, Raspberry Pi Pico-R3_C13"
  Placement = pos=(4.6,0.5,-4.6) rot=(0,0,1;0rad)
  shape: bbox 0.5 x 0.5 x 0.6 mm, 6 faces (baked)
FEATURE [Part::Feature] Part__Feature099  label="SMD Capacitor, Configurable, Raspberry Pi Pico-R3_C038"
  Placement = pos=(4.6,0.5,-4.6) rot=(0,0,1;0rad)
  shape: bbox 0.5 x 0.5 x 0.2 mm, 6 faces (baked)
FEATURE [Part::Feature] Part__Feature100  label="SMD Capacitor, Configurable, Raspberry Pi Pico-R3_C039"
  Placement = pos=(4.6,0.5,-4.6) rot=(0,0,1;0rad)
  shape: bbox 0.5 x 0.5 x 0.2 mm, 6 faces (baked)
FEATURE [App::Part] SMD_Capacitor__Configurable__Raspberry_Pi_Pico_R3_C13  label="SMD Capacitor, Configurable, Raspberry Pi Pico-R3_C040"
  Group = -> [Part__Feature098,Part__Feature099,Part__Feature100]
  Origin = -> Origin029
FEATURE [Part::Feature] Part__Feature101  label="SMD Capacitor, Configurable, Raspberry Pi Pico-R3_C14"
  Placement = pos=(3.2,0.5,-4.6) rot=(0,0,1;0rad)
  shape: bbox 0.5 x 0.5 x 0.6 mm, 6 faces (baked)
FEATURE [Part::Feature] Part__Feature102  label="SMD Capacitor, Configurable, Raspberry Pi Pico-R3_C041"
  Placement = pos=(3.2,0.5,-4.6) rot=(0,0,1;0rad)
  shape: bbox 0.5 x 0.5 x 0.2 mm, 6 faces (baked)
FEATURE [Part::Feature] Part__Feature103  label="SMD Capacitor, Configurable, Raspberry Pi Pico-R3_C042"
  Placement = pos=(3.2,0.5,-4.6) rot=(0,0,1;0rad)
  shape: bbox 0.5 x 0.5 x 0.2 mm, 6 faces (baked)
FEATURE [App::Part] SMD_Capacitor__Configurable__Raspberry_Pi_Pico_R3_C14  label="SMD Capacitor, Configurable, Raspberry Pi Pico-R3_C043"
  Group = -> [Part__Feature101,Part__Feature102,Part__Feature103]
  Origin = -> Origin030
FEATURE [Part::Feature] Part__Feature104  label="SMD Capacitor, Configurable, Raspberry Pi Pico-R3_C15"
  Placement = pos=(-4.5,0.5,-8.8) rot=(0,0,1;0rad)
  shape: bbox 0.3 x 0.3 x 0.4 mm, 6 faces (baked)
FEATURE [Part::Feature] Part__Feature105  label="SMD Capacitor, Configurable, Raspberry Pi Pico-R3_C044"
  Placement = pos=(-4.5,0.5,-8.8) rot=(0,0,1;0rad)
  shape: bbox 0.3 x 0.3 x 0.1 mm, 6 faces (baked)
FEATURE [Part::Feature] Part__Feature106  label="SMD Capacitor, Configurable, Raspberry Pi Pico-R3_C045"
  Placement = pos=(-4.5,0.5,-8.8) rot=(0,0,1;0rad)
  shape: bbox 0.3 x 0.3 x 0.1 mm, 6 faces (baked)
FEATURE [App::Part] SMD_Capacitor__Configurable__Raspberry_Pi_Pico_R3_C15  label="SMD Capacitor, Configurable, Raspberry Pi Pico-R3_C046"
  Group = -> [Part__Feature104,Part__Feature105,Part__Feature106]
  Origin = -> Origin031
FEATURE [Part::Feature] Part__Feature107  label="SMD Capacitor, Configurable, Raspberry Pi Pico-R3_C16"
  Placement = pos=(-4.6,0.5,9.6) rot=(0,0,1;0rad)
  shape: bbox 0.3 x 0.3 x 0.4 mm, 6 faces (baked)
FEATURE [Part::Feature] Part__Feature108  label="SMD Capacitor, Configurable, Raspberry Pi Pico-R3_C047"
  Placement = pos=(-4.6,0.5,9.6) rot=(0,0,1;0rad)
  shape: bbox 0.3 x 0.3 x 0.1 mm, 6 faces (baked)
FEATURE [Part::Feature] Part__Feature109  label="SMD Capacitor, Configurable, Raspberry Pi Pico-R3_C048"
  Placement = pos=(-4.6,0.5,9.6) rot=(0,0,1;0rad)
  shape: bbox 0.3 x 0.3 x 0.1 mm, 6 faces (baked)
FEATURE [App::Part] SMD_Capacitor__Configurable__Raspberry_Pi_Pico_R3_C16  label="SMD Capacitor, Configurable, Raspberry Pi Pico-R3_C049"
  Group = -> [Part__Feature107,Part__Feature108,Part__Feature109]
  Origin = -> Origin032
FEATURE [Part::Feature] Part__Feature110  label="SMD Capacitor, Configurable, Raspberry Pi Pico-R3_C17"
  Placement = pos=(0,0.5,8.5) rot=(0,0,1;0rad)
  shape: bbox 0.3 x 0.3 x 0.4 mm, 6 faces (baked)
FEATURE [Part::Feature] Part__Feature111  label="SMD Capacitor, Configurable, Raspberry Pi Pico-R3_C050"
  Placement = pos=(0,0.5,8.5) rot=(0,0,1;0rad)
  shape: bbox 0.3 x 0.3 x 0.1 mm, 6 faces (baked)
FEATURE [Part::Feature] Part__Feature112  label="SMD Capacitor, Configurable, Raspberry Pi Pico-R3_C051"
  Placement = pos=(0,0.5,8.5) rot=(0,0,1;0rad)
  shape: bbox 0.3 x 0.3 x 0.1 mm, 6 faces (baked)
FEATURE [App::Part] SMD_Capacitor__Configurable__Raspberry_Pi_Pico_R3_C17  label="SMD Capacitor, Configurable, Raspberry Pi Pico-R3_C052"
  Group = -> [Part__Feature110,Part__Feature111,Part__Feature112]
  Origin = -> Origin033
FEATURE [Part::Feature] Part__Feature113  label="SMD Capacitor, Configurable, Raspberry Pi Pico-R3_C18"
  Placement = pos=(-4.7,0.5,-3.1) rot=(0,-1,0;1.5708rad)
  shape: bbox 0.6 x 0.5 x 0.5 mm, 6 faces (baked)
FEATURE [Part::Feature] Part__Feature114  label="SMD Capacitor, Configurable, Raspberry Pi Pico-R3_C053"
  Placement = pos=(-4.7,0.5,-3.1) rot=(0,-1,0;1.5708rad)
  shape: bbox 0.2 x 0.5 x 0.5 mm, 6 faces (baked)
FEATURE [Part::Feature] Part__Feature115  label="SMD Capacitor, Configurable, Raspberry Pi Pico-R3_C054"
  Placement = pos=(-4.7,0.5,-3.1) rot=(0,-1,0;1.5708rad)
  shape: bbox 0.2 x 0.5 x 0.5 mm, 6 faces (baked)
FEATURE [App::Part] SMD_Capacitor__Configurable__Raspberry_Pi_Pico_R3_C18  label="SMD Capacitor, Configurable, Raspberry Pi Pico-R3_C055"
  Group = -> [Part__Feature113,Part__Feature114,Part__Feature115]
  Origin = -> Origin034
FEATURE [App::Part] Raspberry_Pi_Pico_R3  label="Raspberry Pi Pico-R3"
  Group = -> [Part__Feature,MicroUSB_Port__Raspberry_Pi_Pico_R3,Part__Feature008,Part__Feature009,Part__Feature010,Part__Feature011,Part__Feature012,Part__Feature013,Part__Feature014,Part__Feature015,Part__Feature016,SMD_Resistor__Configurable__Raspberry_Pi_Pico_R3_R1,SMD_Resistor__Configurable__Raspberry_Pi_Pico_R3_R2,SMD_Resistor__Configurable__Raspberry_Pi_Pico_R3_R3,+30 more]
  Origin = -> Origin035
  Placement = pos=(1.1,-46.38,1.03e-14) rot=(-0.57735,0.57735,0.57735;4.18879rad)
FEATURE [Sketcher::SketchObject] Sketch001
  AttachmentSupport = -> [XZ_Plane036]
  FullyConstrained = false
  MapMode = 5
  Placement = pos=(0,0,0) rot=(1,0,0;1.5708rad)
  sketch-geometry (7):
    g0: LineSegment StartX=-32.9638 StartY=0 StartZ=0 EndX=-32.9638 EndY=8.29425 EndZ=0
    g1: LineSegment StartX=-32.9638 StartY=8.29425 StartZ=0 EndX=-29.2299 EndY=11.9502 EndZ=0
    g2: LineSegment StartX=-29.2299 StartY=11.9502 StartZ=0 EndX=-0.678443 EndY=11.9502 EndZ=0
    g3: LineSegment StartX=-0.678443 StartY=11.9502 StartZ=0 EndX=24.0566 EndY=8.34824 EndZ=0
    g4: LineSegment StartX=24.0566 StartY=8.34824 StartZ=0 EndX=27.3377 EndY=4.14725 EndZ=0
    g5: LineSegment StartX=27.3377 StartY=4.14725 StartZ=0 EndX=27.3377 EndY=0 EndZ=0
    g6: LineSegment StartX=27.3377 StartY=0 StartZ=0 EndX=-32.9638 EndY=0 EndZ=0
  constraints (12):
    c: PointOnObject(g0,g-1)
    c: Vertical(g0)
    c: Coincident(g0,g1)
    c: Coincident(g1,g2)
    c: Horizontal(g2)
    c: Coincident(g2,g3)
    c: Coincident(g3,g4)
    c: Coincident(g4,g5)
    c: PointOnObject(g5,g-1)
    c: Vertical(g5)
    c: Coincident(g5,g6)
    c: Coincident(g6,g0)
FEATURE [PartDesign::Pad] Pad001
  Direction = (0,-1,2e-16)
  Length = 32.3
  Length2 = 10
  Placement = pos=(0,0,0) rot=(1,0,0;1.5708rad)
  Profile = -> Sketch001
  ReferenceAxis = -> Sketch001 [N_Axis]
  Refine = true
  Suppressed = false
  Type = 0
FEATURE [Sketcher::SketchObject] Sketch002
  AttachmentSupport = -> [Pad001]
  ExternalGeometry = -> [Pad001]
  FullyConstrained = true
  MapMode = 5
  Placement = pos=(-32.9638,0,0) rot=(0.707107,0,-0.707107;3.14159rad)
  sketch-geometry (6):
    g0: LineSegment StartX=-11.9502 StartY=32.3 StartZ=0 EndX=-8.29425 EndY=32.3 EndZ=0
    g1: LineSegment StartX=-8.29425 StartY=32.3 StartZ=0 EndX=-11.9502 EndY=28.47 EndZ=0
    g2: LineSegment StartX=-11.9502 StartY=28.47 StartZ=0 EndX=-11.9502 EndY=32.3 EndZ=0
    g3: LineSegment StartX=-11.9502 StartY=-2.7e-15 StartZ=0 EndX=-11.9502 EndY=3.83 EndZ=0
    g4: LineSegment StartX=-11.9502 StartY=3.83 StartZ=0 EndX=-8.29425 EndY=4e-16 EndZ=0
    g5: LineSegment StartX=-8.29425 StartY=4e-16 StartZ=0 EndX=-11.9502 EndY=-2.7e-15 EndZ=0
  constraints (14):
    c: Coincident(g-3,g0)
    c: Coincident(g0,g-4)
    c: Coincident(g0,g1)
    c: PointOnObject(g1,g-3)
    c: Coincident(g1,g2)
    c: Coincident(g2,g0)
    c: Coincident(g-3,g3)
    c: PointOnObject(g3,g-3)
    c: Coincident(g3,g4)
    c: Coincident(g4,g-4)
    c: Coincident(g4,g5)
    c: Coincident(g5,g3)
    c: Equal(g2,g3)
    c: DistanceY(g2,g2) = 3.83
FEATURE [PartDesign::Pocket] Pocket
  BaseFeature = -> Pad001
  Direction = (1,0,2e-16)
  Length = 5
  Length2 = 5
  Placement = pos=(0,0,0) rot=(1,0,0;1.5708rad)
  Profile = -> Sketch002
  ReferenceAxis = -> Sketch002 [N_Axis]
  Refine = true
  Suppressed = false
  Type = 1
FEATURE [PartDesign::Plane] DatumPlane
  AttachmentOffset = pos=(0,0,0) rot=(0,1,0;1.5708rad)
  AttachmentSupport = -> [Pocket]
  Length = 69.7141
  MapMode = 5
  Placement = pos=(1.68998,5.2e-15,11.6053) rot=(-0.654178,0,0.75634;3.14159rad)
  ResizeMode = 0
  Width = 68.8464
FEATURE [Sketcher::SketchObject] Sketch003
  AttachmentSupport = -> [DatumPlane]
  ExternalGeometry = -> [Pocket]
  FullyConstrained = true
  MapMode = 5
  Placement = pos=(1.68998,5.2e-15,11.6053) rot=(-0.654178,0,0.75634;3.14159rad)
  sketch-geometry (6):
    g0: LineSegment StartX=0 StartY=0 StartZ=0 EndX=0 EndY=3.83 EndZ=0
    g1: LineSegment StartX=0 StartY=3.83 StartZ=0 EndX=3.68434 EndY=-4e-16 EndZ=0
    g2: LineSegment StartX=3.68434 StartY=0 StartZ=0 EndX=0 EndY=0 EndZ=0
    g3: LineSegment StartX=-1.42e-14 StartY=28.47 StartZ=0 EndX=3.68434 EndY=32.3 EndZ=0
    g4: LineSegment StartX=3.68434 StartY=32.3 StartZ=0 EndX=0 EndY=32.3 EndZ=0
    g5: LineSegment StartX=0 StartY=32.3 StartZ=0 EndX=-1.42e-14 EndY=28.47 EndZ=0
  constraints (15):
    c: Coincident(g-1,g0)
    c: Vertical(g0)
    c: Coincident(g0,g1)
    c: Coincident(g1,g2)
    c: Horizontal(g2)
    c: Coincident(g3,g4)
    c: PointOnObject(g4,g-2)
    c: Coincident(g4,g5)
    c: Coincident(g5,g3)
    c: PointOnObject(g4,g-3)
    c: Equal(g2,g4)
    c: Equal(g5,g0)
    c: Coincident(g3,g-3)
    c: Coincident(g3,g-4)
    c: Coincident(g2,g0)
FEATURE [PartDesign::Pocket] Pocket001
  BaseFeature = -> Pocket
  Direction = (0.989563,0,-0.144102)
  Length = 30
  Length2 = 9
  Placement = pos=(0,0,0) rot=(1,0,0;1.5708rad)
  Profile = -> Sketch003
  ReferenceAxis = -> Sketch003 [N_Axis]
  Refine = true
  Suppressed = false
  Type = 4
FEATURE [Sketcher::SketchObject] Sketch004
  AttachmentSupport = -> [Pocket001]
  ExternalGeometry = -> [Pocket001]
  FullyConstrained = true
  MapMode = 5
  Placement = pos=(1.68998,5.2e-15,11.6053) rot=(0.07224,0,0.997387;3.14159rad)
  sketch-geometry (4):
    g0: LineSegment StartX=-21.6025 StartY=27.47 StartZ=0 EndX=-21.6025 EndY=4.83 EndZ=0
    g1: LineSegment StartX=-21.6025 StartY=4.83 StartZ=0 EndX=1.39341 EndY=4.83 EndZ=0
    g2: LineSegment StartX=1.39341 StartY=4.83 StartZ=0 EndX=1.39341 EndY=27.47 EndZ=0
    g3: LineSegment StartX=1.39341 StartY=27.47 StartZ=0 EndX=-21.6025 EndY=27.47 EndZ=0
  constraints (12):
    c: Coincident(g0,g1)
    c: Coincident(g1,g2)
    c: Coincident(g2,g3)
    c: Coincident(g3,g0)
    c: Vertical(g0)
    c: Vertical(g2)
    c: Horizontal(g1)
    c: Horizontal(g3)
    c: DistanceX(g-3,g0) = 1
    c: DistanceY(g0,g-3) = 1
    c: DistanceX(g1,g-4) = 1
    c: DistanceY(g-4,g1) = 1
FEATURE [PartDesign::Pocket] Pocket002
  BaseFeature = -> Pocket001
  Direction = (-0.144102,0,-0.989563)
  Length = 1
  Length2 = 5
  Placement = pos=(0,0,0) rot=(1,0,0;1.5708rad)
  Profile = -> Sketch004
  ReferenceAxis = -> Sketch004 [N_Axis]
  Refine = true
  Suppressed = false
  Type = 0
FEATURE [Sketcher::SketchObject] Sketch005
  AttachmentSupport = -> [Pocket002]
  ExternalGeometry = -> [Pocket002]
  FullyConstrained = true
  MapMode = 5
  Placement = pos=(0,5.3e-15,11.9502) rot=(0,0,1;3.14159rad)
  sketch-geometry (11):
    g0: LineSegment StartX=-21.397 StartY=15.43 StartZ=0 EndX=-21.397 EndY=6.83 EndZ=0
    g1: LineSegment StartX=-21.397 StartY=6.83 StartZ=0 EndX=-6.39705 EndY=6.83 EndZ=0
    g2: LineSegment StartX=-6.39705 StartY=6.83 StartZ=0 EndX=-6.39705 EndY=15.43 EndZ=0
    g3: LineSegment StartX=-6.39705 StartY=15.43 StartZ=0 EndX=-21.397 EndY=15.43 EndZ=0
    g4: LineSegment StartX=-21.397 StartY=25.47 StartZ=0 EndX=-21.397 EndY=16.87 EndZ=0
    g5: LineSegment StartX=-21.397 StartY=16.87 StartZ=0 EndX=-6.39705 EndY=16.87 EndZ=0
    g6: LineSegment StartX=-6.39705 StartY=16.87 StartZ=0 EndX=-6.39705 EndY=25.47 EndZ=0
    g7: LineSegment StartX=-6.39705 StartY=25.47 StartZ=0 EndX=-21.397 EndY=25.47 EndZ=0
    g8: LineSegment StartX=-21.397 StartY=16.87 StartZ=0 EndX=-21.397 EndY=15.43 EndZ=0
    g9: LineSegment StartX=-21.397 StartY=27.47 StartZ=0 EndX=-21.397 EndY=25.47 EndZ=0
    g10: LineSegment StartX=-21.397 StartY=4.83 StartZ=0 EndX=-21.397 EndY=6.83 EndZ=0
  constraints (32):
    c: Coincident(g0,g1)
    c: Coincident(g1,g2)
    c: Coincident(g3,g0)
    c: Vertical(g0)
    c: Vertical(g2)
    c: Horizontal(g1)
    c: Horizontal(g3)
    c: Coincident(g4,g5)
    c: Coincident(g5,g6)
    c: Coincident(g6,g7)
    c: Coincident(g7,g4)
    c: Vertical(g4)
    c: Vertical(g6)
    c: Horizontal(g5)
    c: Horizontal(g7)
    c: Coincident(g8,g4)
    c: Coincident(g8,g0)
    c: Vertical(g8)
    c: Equal(g4,g0)
    c: Equal(g5,g3)
    c: PointOnObject(g9,g-3)
    c: Coincident(g9,g4)
    c: PointOnObject(g10,g-4)
    c: Coincident(g10,g0)
    c: Vertical(g10)
    c: Equal(g9,g10)
    c: Vertical(g9)
    c: DistanceX(g-4,g10) = 1.67
    c: DistanceY(g-4,g0) = 2
    c: Coincident(g3,g2)
    c: DistanceY(g2,g2) = 8.6
    c: DistanceX(g1,g1) = 15
FEATURE [PartDesign::Pocket] Pocket003
  BaseFeature = -> Pocket002
  Direction = (0,0,-1)
  Length = 5
  Length2 = 5
  Placement = pos=(0,0,0) rot=(1,0,0;1.5708rad)
  Profile = -> Sketch005
  ReferenceAxis = -> Sketch005 [N_Axis]
  Refine = true
  Suppressed = false
  Type = 1
FEATURE [PartDesign::Fillet] Fillet
  Base = -> Pocket003 [Edge17,Edge45,Edge46,Edge23,Edge50,Edge49,Edge51,Edge47,Edge42,Edge44,Edge16,Edge21,Edge20,Edge25,Edge24,Edge18,Edge3,Edge2,Edge4,Edge43,Edge48,Edge22,Edge19]
  BaseFeature = -> Pocket003
  Placement = pos=(0,0,0) rot=(1,0,0;1.5708rad)
  Radius = 1.5
  Refine = true
  SupportTransform = false
  Suppressed = false
  UseAllEdges = false
FEATURE [Sketcher::SketchObject] Sketch006
  AttachmentSupport = -> [Fillet]
  ExternalGeometry = -> [Fillet]
  FullyConstrained = true
  MapMode = 5
  Placement = pos=(0,0,0) rot=(1,0,0;3.14159rad)
  sketch-geometry (6):
    g0: LineSegment StartX=-25.0623 StartY=27.4 StartZ=0 EndX=-25.0623 EndY=4.9 EndZ=0
    g1: LineSegment StartX=-25.0623 StartY=4.9 StartZ=0 EndX=26.9377 EndY=4.9 EndZ=0
    g2: LineSegment StartX=26.9377 StartY=4.9 StartZ=0 EndX=26.9377 EndY=27.4 EndZ=0
    g3: LineSegment StartX=26.9377 StartY=27.4 StartZ=0 EndX=-25.0623 EndY=27.4 EndZ=0
    g4: LineSegment StartX=-25.0623 StartY=27.4 StartZ=0 EndX=-25.0623 EndY=32.3 EndZ=0
    g5: LineSegment StartX=-25.0623 StartY=4.9 StartZ=0 EndX=-25.0623 EndY=0 EndZ=0
  constraints (18):
    c: Coincident(g0,g1)
    c: Coincident(g1,g2)
    c: Coincident(g2,g3)
    c: Coincident(g3,g0)
    c: Vertical(g0)
    c: Vertical(g2)
    c: Horizontal(g1)
    c: Horizontal(g3)
    c: DistanceX(g2,g-4) = 0.4
    c: Coincident(g4,g0)
    c: PointOnObject(g4,g-3)
    c: Vertical(g4)
    c: Coincident(g5,g0)
    c: PointOnObject(g5,g-1)
    c: Vertical(g5)
    c: Equal(g5,g4)
    c: DistanceX(g3,g3) = 52
    c: DistanceY(g0,g0) = 22.5
FEATURE [PartDesign::Pocket] Pocket004
  BaseFeature = -> Fillet
  Direction = (0,0,1)
  Length = 4
  Length2 = 5
  Placement = pos=(0,0,0) rot=(1,0,0;1.5708rad)
  Profile = -> Sketch006
  ReferenceAxis = -> Sketch006 [N_Axis]
  Refine = true
  Suppressed = false
  Type = 0
FEATURE [Sketcher::SketchObject] Sketch007
  AttachmentSupport = -> [Pocket004]
  ExternalGeometry = -> [Pocket004]
  FullyConstrained = true
  MapMode = 5
  Placement = pos=(27.3377,0,0) rot=(0.707107,0,0.707107;3.14159rad)
  sketch-geometry (6):
    g0: LineSegment StartX=0 StartY=20.4 StartZ=0 EndX=0 EndY=11.9 EndZ=0
    g1: LineSegment StartX=0 StartY=11.9 StartZ=0 EndX=3.63089 EndY=11.9 EndZ=0
    g2: LineSegment StartX=3.63089 StartY=11.9 StartZ=0 EndX=3.63089 EndY=20.4 EndZ=0
    g3: LineSegment StartX=3.63089 StartY=20.4 StartZ=0 EndX=0 EndY=20.4 EndZ=0
    g4: LineSegment StartX=3.63089 StartY=20.4 StartZ=0 EndX=3.63089 EndY=30.8 EndZ=0
    g5: LineSegment StartX=3.63089 StartY=11.9 StartZ=0 EndX=3.63089 EndY=1.5 EndZ=0
  constraints (16):
    c: Coincident(g0,g1)
    c: Coincident(g1,g2)
    c: Coincident(g2,g3)
    c: Coincident(g3,g0)
    c: Vertical(g0)
    c: Vertical(g2)
    c: Horizontal(g1)
    c: Horizontal(g3)
    c: PointOnObject(g0,g-2)
    c: PointOnObject(g1,g-3)
    c: Coincident(g4,g2)
    c: Coincident(g4,g-3)
    c: Coincident(g5,g1)
    c: Coincident(g5,g-3)
    c: Equal(g5,g4)
    c: DistanceY(g2,g2) = 8.5
FEATURE [PartDesign::Pocket] Pocket005
  BaseFeature = -> Pocket004
  Direction = (-1,0,2e-16)
  Length = 5
  Length2 = 5
  Placement = pos=(0,0,0) rot=(1,0,0;1.5708rad)
  Profile = -> Sketch007
  ReferenceAxis = -> Sketch007 [N_Axis]
  Refine = true
  Suppressed = false
  Type = 0
FEATURE [Sketcher::SketchObject] Sketch008
  AttachmentSupport = -> [Pocket005]
  ExternalGeometry = -> [Pocket005]
  FullyConstrained = true
  MapMode = 5
  Placement = pos=(0,0,4) rot=(1,0,0;3.14159rad)
  sketch-geometry (26):
    g0: LineSegment StartX=26.9377 StartY=23.9 StartZ=0 EndX=22.9377 EndY=23.9 EndZ=0
    g1: LineSegment StartX=22.9377 StartY=23.9 StartZ=0 EndX=22.9377 EndY=20.4 EndZ=0
    g2: LineSegment StartX=22.9377 StartY=20.4 StartZ=0 EndX=26.9377 EndY=20.4 EndZ=0
    g3: LineSegment StartX=26.9377 StartY=20.4 StartZ=0 EndX=26.9377 EndY=23.9 EndZ=0
    g4: LineSegment StartX=26.9377 StartY=11.9 StartZ=0 EndX=22.9377 EndY=11.9 EndZ=0
    g5: LineSegment StartX=22.9377 StartY=11.9 StartZ=0 EndX=22.9377 EndY=8.4 EndZ=0
    g6: LineSegment StartX=22.9377 StartY=8.4 StartZ=0 EndX=26.9377 EndY=8.4 EndZ=0
    g7: LineSegment StartX=26.9377 StartY=8.4 StartZ=0 EndX=26.9377 EndY=11.9 EndZ=0
    g8: Circle CenterX=24.5877 CenterY=21.85 CenterZ=0 NormalX=0 NormalY=0 NormalZ=1 AngleXU=0 Radius=0.75
    g9: Circle CenterX=24.5877 CenterY=10.45 CenterZ=0 NormalX=0 NormalY=0 NormalZ=1 AngleXU=0 Radius=0.75
    g10: LineSegment StartX=24.5877 StartY=21.85 StartZ=0 EndX=24.5877 EndY=20.4 EndZ=0
    g11: LineSegment StartX=24.5877 StartY=20.4 StartZ=0 EndX=24.5877 EndY=11.9 EndZ=0
    g12: LineSegment StartX=24.5877 StartY=11.9 StartZ=0 EndX=24.5877 EndY=10.45 EndZ=0
    g13: LineSegment StartX=24.5877 StartY=21.85 StartZ=0 EndX=-22.4123 EndY=21.85 EndZ=0
    g14: LineSegment StartX=-22.4123 StartY=21.85 StartZ=0 EndX=-22.4123 EndY=10.45 EndZ=0
    g15: LineSegment StartX=-22.4123 StartY=10.45 StartZ=0 EndX=24.5877 EndY=10.45 EndZ=0
    g16: Circle CenterX=-22.4123 CenterY=21.85 CenterZ=0 NormalX=0 NormalY=0 NormalZ=1 AngleXU=0 Radius=0.75
    g17: Circle CenterX=-22.4123 CenterY=10.45 CenterZ=0 NormalX=0 NormalY=0 NormalZ=1 AngleXU=0 Radius=0.75
    g18: LineSegment StartX=-25.0623 StartY=23.9 StartZ=0 EndX=-25.0623 EndY=20.4 EndZ=0
    g19: LineSegment StartX=-25.0623 StartY=20.4 StartZ=0 EndX=-20.3223 EndY=20.4 EndZ=0
    g20: LineSegment StartX=-20.3223 StartY=20.4 StartZ=0 EndX=-20.3223 EndY=23.9 EndZ=0
    g21: LineSegment StartX=-20.3223 StartY=23.9 StartZ=0 EndX=-25.0623 EndY=23.9 EndZ=0
    g22: LineSegment StartX=-25.0623 StartY=11.9 StartZ=0 EndX=-25.0623 EndY=8.4 EndZ=0
    g23: LineSegment StartX=-25.0623 StartY=8.4 StartZ=0 EndX=-20.3223 EndY=8.4 EndZ=0
    g24: LineSegment StartX=-20.3223 StartY=8.4 StartZ=0 EndX=-20.3223 EndY=11.9 EndZ=0
    g25: LineSegment StartX=-20.3223 StartY=11.9 StartZ=0 EndX=-25.0623 EndY=11.9 EndZ=0
  constraints (72):
    c: Coincident(g0,g1)
    c: Coincident(g1,g2)
    c: Coincident(g2,g3)
    c: Coincident(g3,g0)
    c: Horizontal(g0)
    c: Horizontal(g2)
    c: Vertical(g1)
    c: Coincident(g2,g-3)
    c: Coincident(g4,g5)
    c: Coincident(g5,g6)
    c: Coincident(g6,g7)
    c: Coincident(g7,g4)
    c: Horizontal(g4)
    c: Horizontal(g6)
    c: Vertical(g5)
    c: Vertical(g7)
    c: Coincident(g4,g-4)
    c: DistanceY(g5,g5) = 3.5
    c: Equal(g4,g2)
    c: DistanceX(g0,g0) = 4
    c: Vertical(g3)
    c: Equal(g1,g5)
    c: Coincident(g10,g8)
    c: PointOnObject(g10,g2)
    c: Vertical(g10)
    c: Coincident(g11,g10)
    c: PointOnObject(g11,g4)
    c: Vertical(g11)
    c: Coincident(g12,g11)
    c: Coincident(g12,g9)
    c: Vertical(g12)
    c: Equal(g12,g10)
    c: DistanceX(g4,g9) = 1.65
    c: Equal(g8,g9)
    c: Diameter(g8) = 1.5
    c: DistanceY(g10,g10) = 1.45
    c: Coincident(g13,g8)
    c: Horizontal(g13)
    c: Coincident(g14,g13)
    c: Vertical(g14)
    c: Coincident(g15,g14)
    c: Coincident(g15,g9)
    c: Horizontal(g15)
    c: Coincident(g16,g13)
    c: Coincident(g17,g14)
    c: Equal(g16,g17)
    c: Equal(g17,g8)
    c: DistanceX(g13,g13) = 47
    c: Coincident(g18,g19)
    c: Coincident(g19,g20)
    c: Coincident(g20,g21)
    c: Coincident(g21,g18)
    c: Vertical(g18)
    c: Vertical(g20)
    c: Horizontal(g19)
    c: Horizontal(g21)
    c: PointOnObject(g18,g-5)
    c: Coincident(g22,g23)
    c: Coincident(g23,g24)
    c: Coincident(g24,g25)
    c: Coincident(g25,g22)
    c: Vertical(g22)
    c: Vertical(g24)
    c: Horizontal(g23)
    c: Horizontal(g25)
    c: PointOnObject(g22,g-5)
    c: PointOnObject(g19,g2)
    c: PointOnObject(g24,g4)
    c: Equal(g20,g24)
    c: Equal(g24,g1)
    c: Equal(g19,g25)
    c: DistanceX(g19,g19) = 4.74
FEATURE [PartDesign::Pad] Pad002
  BaseFeature = -> Pocket005
  Direction = (0,0,-1)
  Length = 2.75
  Length2 = 10
  Placement = pos=(0,0,0) rot=(1,0,0;1.5708rad)
  Profile = -> Sketch008
  ReferenceAxis = -> Sketch008 [N_Axis]
  Refine = true
  Suppressed = false
  Type = 0
FEATURE [Sketcher::SketchObject] Sketch009
  AttachmentSupport = -> [Pad002]
  ExternalGeometry = -> [Pad002]
  FullyConstrained = true
  MapMode = 5
  Placement = pos=(0,0,4) rot=(1,0,0;3.14159rad)
  sketch-geometry (4):
    g0: LineSegment StartX=4.64705 StartY=26.47 StartZ=0 EndX=4.64705 EndY=5.83 EndZ=0
    g1: LineSegment StartX=4.64705 StartY=5.83 StartZ=0 EndX=22.897 EndY=5.83 EndZ=0
    g2: LineSegment StartX=22.897 StartY=5.83 StartZ=0 EndX=22.897 EndY=26.47 EndZ=0
    g3: LineSegment StartX=22.897 StartY=26.47 StartZ=0 EndX=4.64705 EndY=26.47 EndZ=0
  constraints (12):
    c: Coincident(g0,g1)
    c: Coincident(g1,g2)
    c: Coincident(g2,g3)
    c: Coincident(g3,g0)
    c: Vertical(g0)
    c: Vertical(g2)
    c: Horizontal(g1)
    c: Horizontal(g3)
    c: DistanceX(g0,g-3) = 1.75
    c: DistanceX(g-4,g2) = 1.5
    c: DistanceY(g-3,g0) = 1
    c: DistanceY(g0,g-5) = 1
FEATURE [PartDesign::Pocket] Pocket006
  BaseFeature = -> Pad002
  Direction = (0,0,1)
  Length = 1.5
  Length2 = 5
  Placement = pos=(0,0,0) rot=(1,0,0;1.5708rad)
  Profile = -> Sketch009
  ReferenceAxis = -> Sketch009 [N_Axis]
  Refine = true
  Suppressed = false
  Type = 0
FEATURE [Sketcher::SketchObject] Sketch010
  AttachmentOffset = pos=(0,0,12) rot=(0,0,1;0rad)
  AttachmentSupport = -> [XY_Plane]
  ExternalGeometry = -> [Pad]
  FullyConstrained = true
  MapMode = 5
  Placement = pos=(0,0,12) rot=(0,0,1;0rad)
  sketch-geometry (6):
    g0: LineSegment StartX=5.20138 StartY=-7.8 StartZ=0 EndX=5.20138 EndY=-10.2 EndZ=0
    g1: LineSegment StartX=5.20138 StartY=-10.2 StartZ=0 EndX=22.6514 EndY=-10.2 EndZ=0
    g2: LineSegment StartX=22.6514 StartY=-10.2 StartZ=0 EndX=22.6514 EndY=-7.8 EndZ=0
    g3: LineSegment StartX=22.6514 StartY=-7.8 StartZ=0 EndX=5.20138 EndY=-7.8 EndZ=0
    g4: LineSegment StartX=5.20138 StartY=1.2e-15 StartZ=0 EndX=5.20138 EndY=-7.8 EndZ=0
    g5: LineSegment StartX=5.20138 StartY=-10.2 StartZ=0 EndX=5.20138 EndY=-18 EndZ=0
  constraints (16):
    c: Coincident(g0,g1)
    c: Coincident(g1,g2)
    c: Coincident(g2,g3)
    c: Coincident(g3,g0)
    c: Vertical(g0)
    c: Vertical(g2)
    c: Horizontal(g1)
    c: Horizontal(g3)
    c: PointOnObject(g0,g-3)
    c: PointOnObject(g1,g-4)
    c: Coincident(g4,g-3)
    c: Coincident(g4,g0)
    c: Coincident(g5,g0)
    c: Coincident(g5,g-3)
    c: Equal(g4,g5)
    c: DistanceY(g4,g4) = 7.8
FEATURE [PartDesign::Pocket] Pocket007
  BaseFeature = -> Pad
  Direction = (0,0,-1)
  Length = 6.75
  Length2 = 5
  Placement = pos=(0,0,0) rot=(1,0,0;1.5708rad)
  Profile = -> Sketch010
  ReferenceAxis = -> Sketch010 [N_Axis]
  Refine = true
  Suppressed = false
  Type = 0
FEATURE [PartDesign::Body] Body  label="Botons_vell"
  Group = -> [Sketch,Pad,Sketch010,Pocket007]
  Origin = -> Origin
  Placement = pos=(0,-37.5,0) rot=(0,0,1;0rad)
  Tip = -> Pocket007
FEATURE [Sketcher::SketchObject] Sketch011
  AttachmentSupport = -> [XY_Plane037]
  FullyConstrained = true
  MapMode = 5
  sketch-geometry (4):
    g0: LineSegment StartX=-32.96 StartY=0 StartZ=0 EndX=-32.96 EndY=-32.3 EndZ=0
    g1: LineSegment StartX=-32.96 StartY=-32.3 StartZ=0 EndX=27.34 EndY=-32.3 EndZ=0
    g2: LineSegment StartX=27.34 StartY=-32.3 StartZ=0 EndX=27.34 EndY=0 EndZ=0
    g3: LineSegment StartX=27.34 StartY=0 StartZ=0 EndX=-32.96 EndY=0 EndZ=0
  constraints (12):
    c: Coincident(g0,g1)
    c: Coincident(g1,g2)
    c: Coincident(g2,g3)
    c: Coincident(g3,g0)
    c: Vertical(g0)
    c: Vertical(g2)
    c: Horizontal(g1)
    c: Horizontal(g3)
    c: PointOnObject(g0,g-1)
    c: DistanceX(g1,g1) = 60.3
    c: DistanceX(g2) = 27.34
    c: DistanceY(g0,g0) = 32.3
FEATURE [PartDesign::Pad] Pad003
  Direction = (0,0,1)
  Length = 4.5
  Length2 = 10
  Profile = -> Sketch011
  ReferenceAxis = -> Sketch011 [N_Axis]
  Refine = true
  Reversed = true
  Suppressed = false
  TaperAngle = -40
  Type = 0
FEATURE [PartDesign::Fillet] Fillet001
  Base = -> Pad003 [Edge3,Edge4,Edge12,Edge7,Edge9,Edge10,Edge6,Edge2]
  BaseFeature = -> Pad003
  Radius = 2
  Refine = true
  SupportTransform = false
  Suppressed = false
  UseAllEdges = false
FEATURE [Sketcher::SketchObject] Sketch012
  AttachmentSupport = -> [Fillet001]
  ExternalGeometry = -> [Fillet001]
  FullyConstrained = true
  MapMode = 5
  Placement = pos=(0,0,-4.5) rot=(1,0,0;3.14159rad)
  sketch-geometry (35):
    g0: LineSegment StartX=4.38144 StartY=25.0914 StartZ=0 EndX=4.38144 EndY=21.5914 EndZ=0
    g1: LineSegment StartX=4.88144 StartY=21.0914 StartZ=0 EndX=16.6314 EndY=21.0914 EndZ=0
    g2: LineSegment StartX=17.1314 StartY=21.5914 StartZ=0 EndX=17.1314 EndY=25.0914 EndZ=0
    g3: LineSegment StartX=16.6314 StartY=25.5914 StartZ=0 EndX=4.88144 EndY=25.5914 EndZ=0
    g4: ArcOfCircle CenterX=4.88144 CenterY=25.0914 CenterZ=0 NormalX=0 NormalY=0 NormalZ=1 AngleXU=0 Radius=0.5 StartAngle=1.5708 EndAngle=3.14159
    g5: ArcOfCircle CenterX=4.88144 CenterY=21.5914 CenterZ=0 NormalX=0 NormalY=0 NormalZ=1 AngleXU=0 Radius=0.5 StartAngle=3.14159 EndAngle=4.71239
    g6: ArcOfCircle CenterX=16.6314 CenterY=21.5914 CenterZ=0 NormalX=0 NormalY=0 NormalZ=1 AngleXU=0 Radius=0.5 StartAngle=4.71239 EndAngle=6.28319
    g7: ArcOfCircle CenterX=16.6314 CenterY=25.0914 CenterZ=0 NormalX=0 NormalY=0 NormalZ=1 AngleXU=0 Radius=0.5 StartAngle=1.6e-15 EndAngle=1.5708
    g8: GeomPoint X=4.38144 Y=25.5914 Z=0
    g9: GeomPoint X=17.1314 Y=21.0914 Z=0
    g10: LineSegment StartX=4.38144 StartY=10.7086 StartZ=0 EndX=4.38144 EndY=7.20856 EndZ=0
    g11: LineSegment StartX=4.88144 StartY=6.70856 StartZ=0 EndX=16.6314 EndY=6.70856 EndZ=0
    g12: LineSegment StartX=17.1314 StartY=7.20856 StartZ=0 EndX=17.1314 EndY=10.7086 EndZ=0
    g13: LineSegment StartX=16.6314 StartY=11.2086 StartZ=0 EndX=4.88144 EndY=11.2086 EndZ=0
    g14: ArcOfCircle CenterX=4.88144 CenterY=10.7086 CenterZ=0 NormalX=0 NormalY=0 NormalZ=1 AngleXU=0 Radius=0.5 StartAngle=1.5708 EndAngle=3.14159
    g15: ArcOfCircle CenterX=4.88144 CenterY=7.20856 CenterZ=0 NormalX=0 NormalY=0 NormalZ=1 AngleXU=0 Radius=0.5 StartAngle=3.14159 EndAngle=4.71239
    g16: ArcOfCircle CenterX=16.6314 CenterY=7.20856 CenterZ=0 NormalX=0 NormalY=0 NormalZ=1 AngleXU=0 Radius=0.5 StartAngle=4.71239 EndAngle=6.28319
    g17: ArcOfCircle CenterX=16.6314 CenterY=10.7086 CenterZ=0 NormalX=0 NormalY=0 NormalZ=1 AngleXU=0 Radius=0.5 StartAngle=1.1e-15 EndAngle=1.5708
    g18: GeomPoint X=4.38144 Y=11.2086 Z=0
    g19: GeomPoint X=17.1314 Y=6.70856 Z=0
    g20: LineSegment StartX=-27.3514 StartY=22.025 StartZ=0 EndX=-27.3514 EndY=10.275 EndZ=0
    g21: LineSegment StartX=-26.8514 StartY=9.775 StartZ=0 EndX=-23.3514 EndY=9.775 EndZ=0
    g22: LineSegment StartX=-22.8514 StartY=10.275 StartZ=0 EndX=-22.8514 EndY=22.025 EndZ=0
    g23: LineSegment StartX=-23.3514 StartY=22.525 StartZ=0 EndX=-26.8514 EndY=22.525 EndZ=0
    g24: ArcOfCircle CenterX=-26.8514 CenterY=22.025 CenterZ=0 NormalX=0 NormalY=0 NormalZ=1 AngleXU=0 Radius=0.5 StartAngle=1.5708 EndAngle=3.14159
    g25: ArcOfCircle CenterX=-26.8514 CenterY=10.275 CenterZ=0 NormalX=0 NormalY=0 NormalZ=1 AngleXU=0 Radius=0.5 StartAngle=3.14159 EndAngle=4.71239
    g26: ArcOfCircle CenterX=-23.3514 CenterY=10.275 CenterZ=0 NormalX=0 NormalY=0 NormalZ=1 AngleXU=0 Radius=0.5 StartAngle=4.71239 EndAngle=6.28319
    g27: ArcOfCircle CenterX=-23.3514 CenterY=22.025 CenterZ=0 NormalX=0 NormalY=0 NormalZ=1 AngleXU=0 Radius=0.5 StartAngle=-2.7e-15 EndAngle=1.5708
    g28: GeomPoint X=-27.3514 Y=22.525 Z=0
    g29: GeomPoint X=-22.8514 Y=9.775 Z=0
    g30: LineSegment StartX=4.38144 StartY=25.5914 StartZ=0 EndX=4.38144 EndY=27.5914 EndZ=0
    g31: LineSegment StartX=17.1314 StartY=6.70856 StartZ=0 EndX=17.1314 EndY=4.70856 EndZ=0
    g32: LineSegment StartX=-26.8514 StartY=22.525 StartZ=0 EndX=-26.8514 EndY=27.5914 EndZ=0
    g33: LineSegment StartX=-26.8514 StartY=9.775 StartZ=0 EndX=-26.8514 EndY=4.70856 EndZ=0
    g34: LineSegment StartX=-27.3514 StartY=10.275 StartZ=0 EndX=-28.2514 EndY=10.275 EndZ=0
  constraints (87):
    c: Tangent(g0,g4) = -1.5708
    c: Tangent(g0,g5) = -1.5708
    c: Tangent(g1,g5) = -1.5708
    c: Tangent(g1,g6) = -1.5708
    c: Tangent(g2,g6) = -1.5708
    c: Tangent(g2,g7) = -1.5708
    c: Tangent(g3,g7) = -1.5708
    c: Tangent(g3,g4) = -1.5708
    c: Vertical(g0)
    c: Vertical(g2)
    c: Horizontal(g1)
    c: Horizontal(g3)
    c: Equal(g4,g5)
    c: Equal(g5,g6)
    c: Equal(g6,g7)
    c: PointOnObject(g8,g0)
    c: PointOnObject(g8,g3)
    c: PointOnObject(g9,g1)
    c: PointOnObject(g9,g2)
    c: Radius(g5) = 0.5
    c: Tangent(g10,g14) = -1.5708
    c: Tangent(g10,g15) = -1.5708
    c: Tangent(g11,g15) = -1.5708
    c: Tangent(g11,g16) = -1.5708
    c: Tangent(g12,g16) = -1.5708
    c: Tangent(g12,g17) = -1.5708
    c: Tangent(g13,g17) = -1.5708
    c: Tangent(g13,g14) = -1.5708
    c: Vertical(g10)
    c: Vertical(g12)
    c: Horizontal(g11)
    c: Horizontal(g13)
    c: Equal(g14,g15)
    c: Equal(g15,g16)
    c: Equal(g16,g17)
    c: PointOnObject(g18,g10)
    c: PointOnObject(g18,g13)
    c: PointOnObject(g19,g11)
    c: PointOnObject(g19,g12)
    c: Tangent(g20,g24) = -1.5708
    c: Tangent(g20,g25) = -1.5708
    c: Tangent(g21,g25) = -1.5708
    c: Tangent(g21,g26) = -1.5708
    c: Tangent(g22,g26) = -1.5708
    c: Tangent(g22,g27) = -1.5708
    c: Tangent(g23,g27) = -1.5708
    c: Tangent(g23,g24) = -1.5708
    c: Vertical(g20)
    c: Vertical(g22)
    c: Horizontal(g21)
    c: Horizontal(g23)
    c: Equal(g24,g25)
    c: Equal(g25,g26)
    c: Equal(g26,g27)
    c: PointOnObject(g28,g20)
    c: PointOnObject(g28,g23)
    c: PointOnObject(g29,g21)
    c: PointOnObject(g29,g22)
    c: Equal(g5,g15)
    c: Equal(g15,g25)
    c: PointOnObject(g10,g0)
    c: Equal(g1,g13)
    c: Equal(g10,g0)
    c: Equal(g1,g20)
    c: Equal(g2,g23)
    c: DistanceX(g0,g2) = 12.75
    c: DistanceY(g1,g3) = 4.5
    c: Coincident(g30,g8)
    c: PointOnObject(g30,g-3)
    c: Coincident(g31,g19)
    c: PointOnObject(g31,g-4)
    c: Vertical(g31)
    c: Vertical(g30)
    c: Equal(g30,g31)
    c: Coincident(g32,g23)
    c: PointOnObject(g32,g-3)
    c: Vertical(g32)
    c: Coincident(g33,g21)
    c: PointOnObject(g33,g-4)
    c: Vertical(g33)
    c: Equal(g33,g32)
    c: Coincident(g34,g20)
    c: PointOnObject(g34,g-6)
    c: Horizontal(g34)
    c: DistanceX(g34,g34) = 0.9
    c: DistanceX(g2,g-5) = 5.5
    c: DistanceY(g30,g30) = 2
FEATURE [PartDesign::Pad] Pad004
  BaseFeature = -> Fillet001
  Direction = (0,0,-1)
  Length = 0.5
  Length2 = 10
  Profile = -> Sketch012
  ReferenceAxis = -> Sketch012 [N_Axis]
  Refine = true
  Suppressed = false
  Type = 0
FEATURE [Sketcher::SketchObject] Sketch013
  AttachmentSupport = -> [Pad004]
  ExternalGeometry = -> [Pad004]
  FullyConstrained = true
  MapMode = 5
  Placement = pos=(0,0,-5) rot=(1,0,0;3.14159rad)
  sketch-geometry (30):
    g0: LineSegment StartX=4.78144 StartY=24.9414 StartZ=0 EndX=4.78144 EndY=21.7414 EndZ=0
    g1: LineSegment StartX=5.03144 StartY=21.4914 StartZ=0 EndX=16.4814 EndY=21.4914 EndZ=0
    g2: LineSegment StartX=16.7314 StartY=21.7414 StartZ=0 EndX=16.7314 EndY=24.9414 EndZ=0
    g3: LineSegment StartX=16.4814 StartY=25.1914 StartZ=0 EndX=5.03144 EndY=25.1914 EndZ=0
    g4: ArcOfCircle CenterX=5.03144 CenterY=24.9414 CenterZ=0 NormalX=0 NormalY=0 NormalZ=1 AngleXU=0 Radius=0.25 StartAngle=1.5708 EndAngle=3.14159
    g5: ArcOfCircle CenterX=5.03144 CenterY=21.7414 CenterZ=0 NormalX=0 NormalY=0 NormalZ=1 AngleXU=0 Radius=0.25 StartAngle=3.14159 EndAngle=4.71239
    g6: ArcOfCircle CenterX=16.4814 CenterY=21.7414 CenterZ=0 NormalX=0 NormalY=0 NormalZ=1 AngleXU=0 Radius=0.25 StartAngle=4.71239 EndAngle=6.28319
    g7: ArcOfCircle CenterX=16.4814 CenterY=24.9414 CenterZ=0 NormalX=0 NormalY=0 NormalZ=1 AngleXU=0 Radius=0.25 StartAngle=-5.3e-15 EndAngle=1.5708
    g8: GeomPoint X=4.78144 Y=25.1914 Z=0
    g9: GeomPoint X=16.7314 Y=21.4914 Z=0
    g10: LineSegment StartX=4.78144 StartY=10.5586 StartZ=0 EndX=4.78144 EndY=7.35856 EndZ=0
    g11: LineSegment StartX=5.03144 StartY=7.10856 StartZ=0 EndX=16.4814 EndY=7.10856 EndZ=0
    g12: LineSegment StartX=16.7314 StartY=7.35856 StartZ=0 EndX=16.7314 EndY=10.5586 EndZ=0
    g13: LineSegment StartX=16.4814 StartY=10.8086 StartZ=0 EndX=5.03144 EndY=10.8086 EndZ=0
    g14: ArcOfCircle CenterX=5.03144 CenterY=10.5586 CenterZ=0 NormalX=0 NormalY=0 NormalZ=1 AngleXU=0 Radius=0.25 StartAngle=1.5708 EndAngle=3.14159
    g15: ArcOfCircle CenterX=5.03144 CenterY=7.35856 CenterZ=0 NormalX=0 NormalY=0 NormalZ=1 AngleXU=0 Radius=0.25 StartAngle=3.14159 EndAngle=4.71239
    g16: ArcOfCircle CenterX=16.4814 CenterY=7.35856 CenterZ=0 NormalX=0 NormalY=0 NormalZ=1 AngleXU=0 Radius=0.25 StartAngle=4.71239 EndAngle=6.28319
    g17: ArcOfCircle CenterX=16.4814 CenterY=10.5586 CenterZ=0 NormalX=0 NormalY=0 NormalZ=1 AngleXU=0 Radius=0.25 StartAngle=1e-15 EndAngle=1.5708
    g18: GeomPoint X=4.78144 Y=10.8086 Z=0
    g19: GeomPoint X=16.7314 Y=7.10856 Z=0
    g20: LineSegment StartX=-26.9514 StartY=21.875 StartZ=0 EndX=-26.9514 EndY=10.425 EndZ=0
    g21: LineSegment StartX=-26.7014 StartY=10.175 StartZ=0 EndX=-23.5014 EndY=10.175 EndZ=0
    g22: LineSegment StartX=-23.2514 StartY=10.425 StartZ=0 EndX=-23.2514 EndY=21.875 EndZ=0
    g23: LineSegment StartX=-23.5014 StartY=22.125 StartZ=0 EndX=-26.7014 EndY=22.125 EndZ=0
    g24: ArcOfCircle CenterX=-26.7014 CenterY=21.875 CenterZ=0 NormalX=0 NormalY=0 NormalZ=1 AngleXU=0 Radius=0.25 StartAngle=1.5708 EndAngle=3.14159
    g25: ArcOfCircle CenterX=-26.7014 CenterY=10.425 CenterZ=0 NormalX=0 NormalY=0 NormalZ=1 AngleXU=0 Radius=0.25 StartAngle=3.14159 EndAngle=4.71239
    g26: ArcOfCircle CenterX=-23.5014 CenterY=10.425 CenterZ=0 NormalX=0 NormalY=0 NormalZ=1 AngleXU=0 Radius=0.25 StartAngle=4.71239 EndAngle=6.28319
    g27: ArcOfCircle CenterX=-23.5014 CenterY=21.875 CenterZ=0 NormalX=0 NormalY=0 NormalZ=1 AngleXU=0 Radius=0.25 StartAngle=5.1e-15 EndAngle=1.5708
    g28: GeomPoint X=-26.9514 Y=22.125 Z=0
    g29: GeomPoint X=-23.2514 Y=10.175 Z=0
  constraints (72):
    c: Tangent(g0,g4) = -1.5708
    c: Tangent(g0,g5) = -1.5708
    c: Tangent(g1,g5) = -1.5708
    c: Tangent(g1,g6) = -1.5708
    c: Tangent(g2,g6) = -1.5708
    c: Tangent(g2,g7) = -1.5708
    c: Tangent(g3,g7) = -1.5708
    c: Tangent(g3,g4) = -1.5708
    c: Vertical(g0)
    c: Vertical(g2)
    c: Horizontal(g1)
    c: Horizontal(g3)
    c: Equal(g4,g5)
    c: Equal(g5,g6)
    c: Equal(g6,g7)
    c: PointOnObject(g8,g0)
    c: PointOnObject(g8,g3)
    c: PointOnObject(g9,g1)
    c: PointOnObject(g9,g2)
    c: Radius(g5) = 0.25
    c: Tangent(g10,g14) = -1.5708
    c: Tangent(g10,g15) = -1.5708
    c: Tangent(g11,g15) = -1.5708
    c: Tangent(g11,g16) = -1.5708
    c: Tangent(g12,g16) = -1.5708
    c: Tangent(g12,g17) = -1.5708
    c: Tangent(g13,g17) = -1.5708
    c: Tangent(g13,g14) = -1.5708
    c: Vertical(g10)
    c: Vertical(g12)
    c: Horizontal(g11)
    c: Horizontal(g13)
    c: Equal(g14,g15)
    c: Equal(g15,g16)
    c: Equal(g16,g17)
    c: PointOnObject(g18,g10)
    c: PointOnObject(g18,g13)
    c: PointOnObject(g19,g11)
    c: PointOnObject(g19,g12)
    c: Radius(g15) = 0.25
    c: Tangent(g20,g24) = -1.5708
    c: Tangent(g20,g25) = -1.5708
    c: Tangent(g21,g25) = -1.5708
    c: Tangent(g21,g26) = -1.5708
    c: Tangent(g22,g26) = -1.5708
    c: Tangent(g22,g27) = -1.5708
    c: Tangent(g23,g27) = -1.5708
    c: Tangent(g23,g24) = -1.5708
    c: Vertical(g20)
    c: Vertical(g22)
    c: Horizontal(g21)
    c: Horizontal(g23)
    c: Equal(g24,g25)
    c: Equal(g25,g26)
    c: Equal(g26,g27)
    c: PointOnObject(g28,g20)
    c: PointOnObject(g28,g23)
    c: PointOnObject(g29,g21)
    c: PointOnObject(g29,g22)
    c: Radius(g25) = 0.25
    c: DistanceX(g-3,g8) = 0.4
    c: DistanceY(g8,g-4) = 0.4
    c: DistanceY(g-5,g9) = 0.4
    c: DistanceX(g9,g-6) = 0.4
    c: PointOnObject(g18,g0)
    c: PointOnObject(g12,g2)
    c: Equal(g10,g0)
    c: DistanceY(g13,g-7) = 0.4
    c: Equal(g2,g23)
    c: Equal(g13,g20)
    c: DistanceY(g23,g-8) = 0.4
    c: DistanceX(g-9,g28) = 0.4
FEATURE [Sketcher::SketchObject] Sketch014
  FullyConstrained = true
  MapMode = 5
  sketch-geometry (8):
    g0: LineSegment StartX=-22.41 StartY=-10.45 StartZ=0 EndX=-22.41 EndY=-21.85 EndZ=0
    g1: LineSegment StartX=-22.41 StartY=-21.85 StartZ=0 EndX=24.59 EndY=-21.85 EndZ=0
    g2: LineSegment StartX=24.59 StartY=-21.85 StartZ=0 EndX=24.59 EndY=-10.45 EndZ=0
    g3: LineSegment StartX=24.59 StartY=-10.45 StartZ=0 EndX=-22.41 EndY=-10.45 EndZ=0
    g4: Circle CenterX=-22.41 CenterY=-10.45 CenterZ=0 NormalX=0 NormalY=0 NormalZ=1 AngleXU=0 Radius=2
    g5: Circle CenterX=-22.41 CenterY=-21.85 CenterZ=0 NormalX=0 NormalY=0 NormalZ=1 AngleXU=0 Radius=2
    g6: Circle CenterX=24.59 CenterY=-10.45 CenterZ=0 NormalX=0 NormalY=0 NormalZ=1 AngleXU=0 Radius=2
    g7: Circle CenterX=24.59 CenterY=-21.85 CenterZ=0 NormalX=0 NormalY=0 NormalZ=1 AngleXU=0 Radius=2
  constraints (20):
    c: Coincident(g0,g1)
    c: Coincident(g1,g2)
    c: Coincident(g2,g3)
    c: Coincident(g3,g0)
    c: Vertical(g0)
    c: Vertical(g2)
    c: Horizontal(g1)
    c: Horizontal(g3)
    c: Coincident(g4,g0)
    c: Coincident(g5,g0)
    c: Coincident(g6,g2)
    c: Coincident(g7,g1)
    c: Equal(g4,g5)
    c: Equal(g5,g7)
    c: Equal(g7,g6)
    c: Diameter(g4) = 4
    c: DistanceX(g4) = -22.41
    c: DistanceY(g4) = -10.45
    c: DistanceX(g1,g1) = 47
    c: DistanceY(g2,g2) = 11.4
FEATURE [PartDesign::Pad] Pad005
  BaseFeature = -> Pad004
  Direction = (0,0,-1)
  Length = 0.4
  Length2 = 10
  Profile = -> Sketch013
  ReferenceAxis = -> Sketch013 [N_Axis]
  Refine = true
  Suppressed = false
  Type = 0
FEATURE [Sketcher::SketchObject] Sketch015
  FullyConstrained = true
  MapMode = 5
  sketch-geometry (8):
    g0: LineSegment StartX=-22.41 StartY=-10.45 StartZ=0 EndX=-22.41 EndY=-21.85 EndZ=0
    g1: LineSegment StartX=-22.41 StartY=-21.85 StartZ=0 EndX=24.59 EndY=-21.85 EndZ=0
    g2: LineSegment StartX=24.59 StartY=-21.85 StartZ=0 EndX=24.59 EndY=-10.45 EndZ=0
    g3: LineSegment StartX=24.59 StartY=-10.45 StartZ=0 EndX=-22.41 EndY=-10.45 EndZ=0
    g4: Circle CenterX=-22.41 CenterY=-10.45 CenterZ=0 NormalX=0 NormalY=0 NormalZ=1 AngleXU=0 Radius=2
    g5: Circle CenterX=-22.41 CenterY=-21.85 CenterZ=0 NormalX=0 NormalY=0 NormalZ=1 AngleXU=0 Radius=2
    g6: Circle CenterX=24.59 CenterY=-10.45 CenterZ=0 NormalX=0 NormalY=0 NormalZ=1 AngleXU=0 Radius=2
    g7: Circle CenterX=24.59 CenterY=-21.85 CenterZ=0 NormalX=0 NormalY=0 NormalZ=1 AngleXU=0 Radius=2
  constraints (20):
    c: Coincident(g0,g1)
    c: Coincident(g1,g2)
    c: Coincident(g2,g3)
    c: Coincident(g3,g0)
    c: Vertical(g0)
    c: Vertical(g2)
    c: Horizontal(g1)
    c: Horizontal(g3)
    c: Coincident(g4,g0)
    c: Coincident(g5,g0)
    c: Coincident(g6,g2)
    c: Coincident(g7,g1)
    c: Equal(g4,g5)
    c: Equal(g5,g7)
    c: Equal(g7,g6)
    c: Diameter(g4) = 4
    c: DistanceX(g4) = -22.41
    c: DistanceY(g4) = -10.45
    c: DistanceX(g1,g1) = 47
    c: DistanceY(g2,g2) = 11.4
FEATURE [PartDesign::Pocket] Pocket008
  BaseFeature = -> Pad005
  Direction = (0,0,-1)
  Length = 2
  Length2 = 5
  Profile = -> Sketch014
  ReferenceAxis = -> Sketch014 [N_Axis]
  Refine = true
  Suppressed = false
  Type = 0
FEATURE [PartDesign::Pocket] Pocket009
  BaseFeature = -> Pocket008
  Direction = (0,0,-1)
  Length = 1
  Length2 = 5
  Profile = -> Sketch015
  ReferenceAxis = -> Sketch015 [N_Axis]
  Refine = true
  Suppressed = false
  TaperAngle = -17.5
  Type = 0
FEATURE [Sketcher::SketchObject] Sketch016
  AttachmentSupport = -> [XZ_Plane038]
  FullyConstrained = true
  MapMode = 5
  Placement = pos=(0,0,0) rot=(1,0,0;1.5708rad)
  sketch-geometry (14):
    g0: LineSegment StartX=21.1514 StartY=8.48067 StartZ=0 EndX=15.1514 EndY=9.36067 EndZ=0
    g1: LineSegment StartX=15.1514 StartY=9.36067 StartZ=0 EndX=15.1514 EndY=8.76067 EndZ=0
    g2: LineSegment StartX=15.1514 StartY=8.76067 StartZ=0 EndX=6.70138 EndY=10 EndZ=0
    g3: LineSegment StartX=6.70138 StartY=10 StartZ=0 EndX=6.70138 EndY=5.25 EndZ=0
    g4: LineSegment StartX=6.70138 StartY=5.25 StartZ=0 EndX=5.20138 EndY=5.25 EndZ=0
    g5: LineSegment StartX=5.20138 StartY=5.25 StartZ=0 EndX=5.20138 EndY=4.25 EndZ=0
    g6: LineSegment StartX=5.20138 StartY=4.25 StartZ=0 EndX=11.74 EndY=4.25 EndZ=0
    g7: LineSegment StartX=11.74 StartY=4.25 StartZ=0 EndX=11.74 EndY=3.5 EndZ=0
    g8: LineSegment StartX=11.74 StartY=3.5 StartZ=0 EndX=17.37 EndY=3.5 EndZ=0
    g9: LineSegment StartX=17.37 StartY=3.5 StartZ=0 EndX=17.37 EndY=4.25 EndZ=0
    g10: LineSegment StartX=17.37 StartY=4.25 StartZ=0 EndX=22.6514 EndY=4.25 EndZ=0
    g11: LineSegment StartX=22.6514 StartY=4.25 StartZ=0 EndX=22.6514 EndY=5.25 EndZ=0
    g12: LineSegment StartX=22.6514 StartY=5.25 StartZ=0 EndX=21.1514 EndY=5.25 EndZ=0
    g13: LineSegment StartX=21.1514 StartY=5.25 StartZ=0 EndX=21.1514 EndY=8.48067 EndZ=0
  constraints (42):
    c: Coincident(g0,g1)
    c: Vertical(g1)
    c: Coincident(g1,g2)
    c: Coincident(g2,g3)
    c: Vertical(g3)
    c: Coincident(g3,g4)
    c: Coincident(g4,g5)
    c: Vertical(g5)
    c: Coincident(g5,g6)
    c: Horizontal(g6)
    c: Coincident(g6,g7)
    c: Coincident(g7,g8)
    c: Horizontal(g8)
    c: Coincident(g8,g9)
    c: Coincident(g9,g10)
    c: Coincident(g10,g11)
    c: Vertical(g11)
    c: Coincident(g11,g12)
    c: Coincident(g12,g13)
    c: Coincident(g13,g0)
    c: Vertical(g13)
    c: Parallel(g0,g2)
    c: DistanceX(g0) = 21.1514
    c: DistanceX(g0,g0) = 6
    c: DistanceX(g2,g2) = 8.45
    c: DistanceY(g0,g0) = 0.88
    c: DistanceY(g1,g1) = 0.6
    c: Vertical(g9)
    c: Vertical(g7)
    c: Horizontal(g10)
    c: Equal(g7,g9)
    c: DistanceX(g7) = 11.74
    c: DistanceX(g8,g8) = 5.63
    c: DistanceX(g4,g3) = 1.5
    c: Horizontal(g12)
    c: DistanceX(g12,g12) = 1.5
    c: Horizontal(g4)
    c: PointOnObject(g3,g12)
    c: DistanceY(g5,g5) = 1
    c: DistanceY(g7,g7) = 0.75
    c: DistanceY(g3,g3) = 4.75
    c: DistanceY(g10) = 4.25
FEATURE [PartDesign::Pad] Pad006
  Direction = (0,-1,2e-16)
  Length = 18
  Length2 = 10
  Placement = pos=(0,0,0) rot=(1,0,0;1.5708rad)
  Profile = -> Sketch016
  ReferenceAxis = -> Sketch016 [N_Axis]
  Refine = true
  Suppressed = false
  Type = 0
FEATURE [Sketcher::SketchObject] Sketch017
  AttachmentOffset = pos=(0,0,12) rot=(0,0,1;0rad)
  AttachmentSupport = -> [XY_Plane038]
  ExternalGeometry = -> [Pad006]
  FullyConstrained = true
  MapMode = 5
  Placement = pos=(0,0,12) rot=(0,0,1;0rad)
  sketch-geometry (6):
    g0: LineSegment StartX=5.20138 StartY=-7.8 StartZ=0 EndX=5.20138 EndY=-10.2 EndZ=0
    g1: LineSegment StartX=5.20138 StartY=-10.2 StartZ=0 EndX=22.6514 EndY=-10.2 EndZ=0
    g2: LineSegment StartX=22.6514 StartY=-10.2 StartZ=0 EndX=22.6514 EndY=-7.8 EndZ=0
    g3: LineSegment StartX=22.6514 StartY=-7.8 StartZ=0 EndX=5.20138 EndY=-7.8 EndZ=0
    g4: LineSegment StartX=5.20138 StartY=1.2e-15 StartZ=0 EndX=5.20138 EndY=-7.8 EndZ=0
    g5: LineSegment StartX=5.20138 StartY=-10.2 StartZ=0 EndX=5.20138 EndY=-18 EndZ=0
  constraints (16):
    c: Coincident(g0,g1)
    c: Coincident(g1,g2)
    c: Coincident(g2,g3)
    c: Coincident(g3,g0)
    c: Vertical(g0)
    c: Vertical(g2)
    c: Horizontal(g1)
    c: Horizontal(g3)
    c: PointOnObject(g0,g-3)
    c: PointOnObject(g1,g-4)
    c: Coincident(g4,g-3)
    c: Coincident(g4,g0)
    c: Coincident(g5,g0)
    c: Coincident(g5,g-3)
    c: Equal(g4,g5)
    c: DistanceY(g4,g4) = 7.8
FEATURE [PartDesign::Pocket] Pocket010
  BaseFeature = -> Pad006
  Direction = (0,0,-1)
  Length = 6.75
  Length2 = 5
  Placement = pos=(0,0,0) rot=(1,0,0;1.5708rad)
  Profile = -> Sketch017
  ReferenceAxis = -> Sketch017 [N_Axis]
  Refine = true
  Suppressed = false
  Type = 0
FEATURE [Sketcher::SketchObject] Sketch018
  AttachmentSupport = -> [Pocket010]
  ExternalGeometry = -> [Pocket010]
  FullyConstrained = true
  MapMode = 5
  Placement = pos=(0,1.5e-15,3.5) rot=(1,0,0;3.14159rad)
  sketch-geometry (4):
    g0: LineSegment StartX=11.74 StartY=18 StartZ=0 EndX=11.74 EndY=10.2 EndZ=0
    g1: LineSegment StartX=11.74 StartY=10.2 StartZ=0 EndX=17.37 EndY=10.2 EndZ=0
    g2: LineSegment StartX=17.37 StartY=10.2 StartZ=0 EndX=17.37 EndY=18 EndZ=0
    g3: LineSegment StartX=17.37 StartY=18 StartZ=0 EndX=11.74 EndY=18 EndZ=0
  constraints (10):
    c: Coincident(g0,g1)
    c: Coincident(g1,g2)
    c: Coincident(g2,g3)
    c: Coincident(g3,g0)
    c: Vertical(g0)
    c: Vertical(g2)
    c: Horizontal(g1)
    c: Coincident(g0,g-3)
    c: PointOnObject(g1,g-4)
    c: Coincident(g2,g-3)
FEATURE [PartDesign::Pad] Pad007
  BaseFeature = -> Pocket010
  Direction = (0,0,-1)
  Length = 0.66
  Length2 = 10
  Placement = pos=(0,0,0) rot=(1,0,0;1.5708rad)
  Profile = -> Sketch018
  ReferenceAxis = -> Sketch018 [N_Axis]
  Refine = true
  Suppressed = false
  Type = 0
FEATURE [PartDesign::Body] Body003  label="Botons"
  Group = -> [Sketch016,Pad006,Sketch017,Pocket010,Sketch018,Pad007]
  Origin = -> Origin038
  Placement = pos=(0,-37.5,0) rot=(0,0,1;0rad)
  Tip = -> Pad007
FEATURE [PartDesign::Pad] Pad008
  BaseFeature = -> Pocket006
  Direction = (0,1,-4e-16)
  Length = 10
  Length2 = 10
  Placement = pos=(0,0,0) rot=(1,0,0;1.5708rad)
  Profile = -> Pocket006 [Face42]
  Refine = true
  Suppressed = false
  Type = 3
  UpToFace = -> Pocket006 [Face15]
FEATURE [PartDesign::Pad] Pad009
  BaseFeature = -> Pad008
  Direction = (0,-1,3e-16)
  Length = 10
  Length2 = 10
  Placement = pos=(0,0,0) rot=(1,0,0;1.5708rad)
  Profile = -> Pad008 [Face34]
  Refine = true
  Suppressed = false
  Type = 3
  UpToFace = -> Pad008 [Face13]
FEATURE [Part::Box] Box  label="Cub"
  AttacherType = Attacher::AttachEngine3D
  Height = 1
  Length = 53
  Placement = pos=(-25.4,-58,0) rot=(0,0,1;0rad)
  Width = 23
FEATURE [Sketcher::SketchObject] Sketch019
  AttachmentSupport = -> [XZ_Plane039]
  FullyConstrained = true
  MapMode = 5
  Placement = pos=(0,0,0) rot=(1,0,0;1.5708rad)
  sketch-geometry (10):
    g0: LineSegment StartX=21.1514 StartY=8.48067 StartZ=0 EndX=15.1514 EndY=9.36067 EndZ=0
    g1: LineSegment StartX=15.1514 StartY=9.36067 StartZ=0 EndX=15.1514 EndY=8.76067 EndZ=0
    g2: LineSegment StartX=15.1514 StartY=8.76067 StartZ=0 EndX=6.70138 EndY=10 EndZ=0
    g3: LineSegment StartX=6.70138 StartY=10 StartZ=0 EndX=6.70138 EndY=5.25 EndZ=0
    g4: LineSegment StartX=6.70138 StartY=5.25 StartZ=0 EndX=5.20138 EndY=5.25 EndZ=0
    g5: LineSegment StartX=5.20138 StartY=5.25 StartZ=0 EndX=5.20138 EndY=4.25 EndZ=0
    g6: LineSegment StartX=5.20138 StartY=4.25 StartZ=0 EndX=22.6514 EndY=4.25 EndZ=0
    g7: LineSegment StartX=22.6514 StartY=4.25 StartZ=0 EndX=22.6514 EndY=5.25 EndZ=0
    g8: LineSegment StartX=22.6514 StartY=5.25 StartZ=0 EndX=21.1514 EndY=5.25 EndZ=0
    g9: LineSegment StartX=21.1514 StartY=5.25 StartZ=0 EndX=21.1514 EndY=8.48067 EndZ=0
  constraints (30):
    c: Coincident(g0,g1)
    c: Vertical(g1)
    c: Coincident(g1,g2)
    c: Coincident(g2,g3)
    c: Vertical(g3)
    c: Coincident(g3,g4)
    c: Coincident(g4,g5)
    c: Vertical(g5)
    c: Coincident(g5,g6)
    c: Horizontal(g6)
    c: Vertical(g7)
    c: Coincident(g7,g8)
    c: Coincident(g8,g9)
    c: Coincident(g9,g0)
    c: Vertical(g9)
    c: Parallel(g0,g2)
    c: DistanceX(g0) = 21.1514
    c: DistanceX(g0,g0) = 6
    c: DistanceX(g2,g2) = 8.45
    c: DistanceY(g0,g0) = 0.88
    c: DistanceY(g1,g1) = 0.6
    c: DistanceX(g4,g3) = 1.5
    c: Horizontal(g8)
    c: DistanceX(g8,g8) = 1.5
    c: Horizontal(g4)
    c: PointOnObject(g3,g8)
    c: DistanceY(g5,g5) = 1
    c: DistanceY(g3,g3) = 4.75
    c: Coincident(g6,g7)
    c: DistanceY(g6) = 4.25
FEATURE [PartDesign::Pad] Pad010
  Direction = (0,-1,2e-16)
  Length = 18
  Length2 = 10
  Placement = pos=(0,0,0) rot=(1,0,0;1.5708rad)
  Profile = -> Sketch019
  ReferenceAxis = -> Sketch019 [N_Axis]
  Refine = true
  Suppressed = false
  Type = 0
FEATURE [Sketcher::SketchObject] Sketch020
  AttachmentOffset = pos=(0,0,12) rot=(0,0,1;0rad)
  AttachmentSupport = -> [XY_Plane039]
  ExternalGeometry = -> [Pad010]
  FullyConstrained = false
  MapMode = 5
  Placement = pos=(0,0,12) rot=(0,0,1;0rad)
  sketch-geometry (6):
    g0: LineSegment StartX=5.20138 StartY=-7.8 StartZ=0 EndX=5.20138 EndY=-10.2 EndZ=0
    g1: LineSegment StartX=5.20138 StartY=-10.2 StartZ=0 EndX=22.6514 EndY=-10.2 EndZ=0
    g2: LineSegment StartX=22.6514 StartY=-10.2 StartZ=0 EndX=22.6514 EndY=-7.8 EndZ=0
    g3: LineSegment StartX=22.6514 StartY=-7.8 StartZ=0 EndX=5.20138 EndY=-7.8 EndZ=0
    g4: LineSegment StartX=5.20138 StartY=1.2e-15 StartZ=0 EndX=5.20138 EndY=-7.8 EndZ=0
    g5: LineSegment StartX=5.20138 StartY=-10.2 StartZ=0 EndX=5.20138 EndY=-18 EndZ=0
  constraints (12):
    c: Coincident(g0,g1)
    c: Coincident(g1,g2)
    c: Coincident(g2,g3)
    c: Coincident(g3,g0)
    c: Vertical(g0)
    c: Vertical(g2)
    c: Horizontal(g1)
    c: Horizontal(g3)
    c: Coincident(g4,g0)
    c: Coincident(g5,g0)
    c: Equal(g4,g5)
    c: DistanceY(g4,g4) = 7.8
FEATURE [PartDesign::Pocket] Pocket011
  BaseFeature = -> Pad010
  Direction = (0,0,-1)
  Length = 6.75
  Length2 = 5
  Placement = pos=(0,0,0) rot=(1,0,0;1.5708rad)
  Profile = -> Sketch020
  ReferenceAxis = -> Sketch020 [N_Axis]
  Refine = true
  Suppressed = false
  Type = 0
FEATURE [Sketcher::SketchObject] Sketch021
  AttachmentSupport = -> [Pocket011]
  ExternalGeometry = -> [Pocket011]
  FullyConstrained = true
  MapMode = 5
  Placement = pos=(0,2.8e-15,4.25) rot=(1,0,0;3.14159rad)
  sketch-geometry (4):
    g0: LineSegment StartX=5.20138 StartY=0 StartZ=0 EndX=11.2014 EndY=0 EndZ=0
    g1: LineSegment StartX=11.2014 StartY=0 StartZ=0 EndX=11.2014 EndY=6 EndZ=0
    g2: LineSegment StartX=11.2014 StartY=6 StartZ=0 EndX=5.20138 EndY=6 EndZ=0
    g3: LineSegment StartX=5.20138 StartY=6 StartZ=0 EndX=5.20138 EndY=0 EndZ=0
  constraints (11):
    c: Coincident(g0,g1)
    c: Coincident(g1,g2)
    c: Coincident(g2,g3)
    c: Coincident(g3,g0)
    c: Horizontal(g0)
    c: Horizontal(g2)
    c: Vertical(g1)
    c: Vertical(g3)
    c: Coincident(g0,g-3)
    c: DistanceY(g3,g3) = 6
    c: DistanceX(g2,g2) = 6
FEATURE [PartDesign::Pad] Pad011
  BaseFeature = -> Pocket011
  Direction = (0,0,-1)
  Length = 0.75
  Length2 = 10
  Placement = pos=(0,0,0) rot=(1,0,0;1.5708rad)
  Profile = -> Sketch021
  ReferenceAxis = -> Sketch021 [N_Axis]
  Refine = true
  Suppressed = false
  Type = 0
FEATURE [Sketcher::SketchObject] Sketch022
  AttachmentSupport = -> [Pad011]
  ExternalGeometry = -> [Pad011]
  FullyConstrained = true
  MapMode = 5
  Placement = pos=(0,2.8e-15,4.25) rot=(1,0,0;3.14159rad)
  sketch-geometry (6):
    g0: LineSegment StartX=22.6514 StartY=4.25 StartZ=0 EndX=22.6514 EndY=13.75 EndZ=0
    g1: LineSegment StartX=22.6514 StartY=13.75 StartZ=0 EndX=18.6514 EndY=13.75 EndZ=0
    g2: LineSegment StartX=18.6514 StartY=13.75 StartZ=0 EndX=18.6514 EndY=4.25 EndZ=0
    g3: LineSegment StartX=18.6514 StartY=4.25 StartZ=0 EndX=22.6514 EndY=4.25 EndZ=0
    g4: LineSegment StartX=22.6514 StartY=13.75 StartZ=0 EndX=22.6514 EndY=18 EndZ=0
    g5: LineSegment StartX=22.6514 StartY=4.25 StartZ=0 EndX=22.6514 EndY=0 EndZ=0
  constraints (16):
    c: Coincident(g0,g1)
    c: Coincident(g1,g2)
    c: Coincident(g2,g3)
    c: Coincident(g3,g0)
    c: Vertical(g0)
    c: Vertical(g2)
    c: Horizontal(g1)
    c: Horizontal(g3)
    c: PointOnObject(g0,g-3)
    c: Coincident(g4,g0)
    c: Coincident(g4,g-3)
    c: Coincident(g5,g0)
    c: Coincident(g5,g-3)
    c: Equal(g5,g4)
    c: DistanceY(g0,g0) = 9.5
    c: DistanceX(g3,g3) = 4
FEATURE [PartDesign::Pocket] Pocket012
  BaseFeature = -> Pad011
  Direction = (0,0,1)
  Length = 1
  Length2 = 5
  Placement = pos=(0,0,0) rot=(1,0,0;1.5708rad)
  Profile = -> Sketch022
  ReferenceAxis = -> Sketch022 [N_Axis]
  Refine = true
  Suppressed = false
  Type = 0
FEATURE [PartDesign::Chamfer] Chamfer
  Angle = 45
  Base = -> Pocket012 [Edge43,Edge42,Edge72,Edge59]
  BaseFeature = -> Pocket012
  ChamferType = 0
  FlipDirection = false
  Placement = pos=(0,0,0) rot=(1,0,0;1.5708rad)
  Refine = true
  Size = 1
  Size2 = 1
  SupportTransform = false
  Suppressed = false
  UseAllEdges = false
FEATURE [Sketcher::SketchObject] Sketch023
  AttachmentSupport = -> [Pad009]
  ExternalGeometry = -> [Pad009]
  FullyConstrained = true
  MapMode = 5
  Placement = pos=(0,0,4) rot=(1,0,0;3.14159rad)
  sketch-geometry (3):
    g0: Circle CenterX=-17.0623 CenterY=16.15 CenterZ=0 NormalX=0 NormalY=0 NormalZ=1 AngleXU=0 Radius=3.57143
    g1: LineSegment StartX=-17.0623 StartY=16.15 StartZ=0 EndX=-17.0623 EndY=27.4 EndZ=0
    g2: LineSegment StartX=-17.0623 StartY=16.15 StartZ=0 EndX=-17.0623 EndY=4.9 EndZ=0
  constraints (9):
    c: Coincident(g1,g0)
    c: PointOnObject(g1,g-3)
    c: Vertical(g1)
    c: Coincident(g2,g0)
    c: PointOnObject(g2,g-4)
    c: Vertical(g2)
    c: Equal(g2,g1)
    c: DistanceX(g-3,g1) = 8
    c: Diameter(g0) = 7.14286
FEATURE [PartDesign::Pocket] Pocket013
  BaseFeature = -> Pad009
  Direction = (0,0,1)
  Length = 7.3
  Length2 = 5
  Placement = pos=(0,0,0) rot=(1,0,0;1.5708rad)
  Profile = -> Sketch023
  ReferenceAxis = -> Sketch023 [N_Axis]
  Refine = true
  Suppressed = false
  TaperAngle = -16
  Type = 0
FEATURE [PartDesign::Chamfer] Chamfer001
  Angle = 45
  Base = -> Pocket013 [Edge101,Edge106,Edge119,Edge120,Edge114,Edge100,Edge125,Edge107,Edge102,Edge104]
  BaseFeature = -> Pocket013
  ChamferType = 0
  FlipDirection = false
  Placement = pos=(0,0,0) rot=(1,0,0;1.5708rad)
  Refine = true
  Size = 1
  Size2 = 1
  SupportTransform = false
  Suppressed = false
  UseAllEdges = false
FEATURE [PartDesign::Pad] Pad012
  BaseFeature = -> Chamfer
  Direction = (0,-1,0)
  Length = 12
  Length2 = 10
  Placement = pos=(0,0,0) rot=(1,0,0;1.5708rad)
  Profile = -> Chamfer [Face23]
  Refine = true
  Suppressed = false
  Type = 0
FEATURE [PartDesign::Pad] Pad013
  BaseFeature = -> Pad012
  Direction = (0,-2e-16,-1)
  Length = 1
  Length2 = 10
  Placement = pos=(0,0,0) rot=(1,0,0;1.5708rad)
  Profile = -> Pad012 [Face7]
  Refine = true
  Suppressed = false
  Type = 3
  UpToFace = -> Pad012 [Face32]
FEATURE [PartDesign::Pad] Pad014
  BaseFeature = -> Pad013
  Direction = (0,2e-16,-1)
  Length = 0.5
  Length2 = 10
  Placement = pos=(0,0,0) rot=(1,0,0;1.5708rad)
  Profile = -> Pad013 [Face25]
  Refine = true
  Suppressed = false
  Type = 0
FEATURE [PartDesign::Body] Body004  label="Botons_llarg"
  Group = -> [Sketch019,Pad010,Sketch020,Pocket011,Sketch021,Pad011,Sketch022,Pocket012,Chamfer,Pad012,Pad013,Pad014]
  Origin = -> Origin039
  Placement = pos=(0,-37.5,0) rot=(0,0,1;0rad)
  Tip = -> Pad014
FEATURE [Sketcher::SketchObject] Sketch024
  AttachmentSupport = -> [Chamfer001]
  ExternalGeometry = -> [Chamfer001]
  FullyConstrained = true
  MapMode = 5
  Placement = pos=(0,0,0) rot=(1,0,0;3.14159rad)
  sketch-geometry (13):
    g0: LineSegment StartX=25.3377 StartY=30.8 StartZ=0 EndX=25.3377 EndY=29 EndZ=0
    g1: LineSegment StartX=25.3377 StartY=29 StartZ=0 EndX=-26.9638 EndY=29 EndZ=0
    g2: LineSegment StartX=-26.9638 StartY=29 StartZ=0 EndX=-26.9638 EndY=3.3 EndZ=0
    g3: LineSegment StartX=-26.9638 StartY=3.3 StartZ=0 EndX=25.3377 EndY=3.3 EndZ=0
    g4: LineSegment StartX=25.3377 StartY=3.3 StartZ=0 EndX=25.3377 EndY=1.5 EndZ=0
    g5: LineSegment StartX=25.3377 StartY=1.5 StartZ=0 EndX=-29.9638 EndY=1.5 EndZ=0
    g6: LineSegment StartX=-29.9638 StartY=1.5 StartZ=0 EndX=-29.9638 EndY=30.8 EndZ=0
    g7: LineSegment StartX=-29.9638 StartY=30.8 StartZ=0 EndX=25.3377 EndY=30.8 EndZ=0
    g8: LineSegment StartX=-29.9638 StartY=30.8 StartZ=0 EndX=-29.9638 EndY=32.3 EndZ=0
    g9: LineSegment StartX=-29.9638 StartY=1.5 StartZ=0 EndX=-29.9638 EndY=0 EndZ=0
    g10: LineSegment StartX=-29.9638 StartY=1.5 StartZ=0 EndX=-32.9638 EndY=1.5 EndZ=0
    g11: LineSegment StartX=25.3377 StartY=3.3 StartZ=0 EndX=27.3377 EndY=3.3 EndZ=0
    g12: LineSegment StartX=25.3377 StartY=29 StartZ=0 EndX=27.3377 EndY=29 EndZ=0
  constraints (39):
    c: Vertical(g0)
    c: Coincident(g0,g1)
    c: Horizontal(g1)
    c: Coincident(g1,g2)
    c: Vertical(g2)
    c: Coincident(g2,g3)
    c: Horizontal(g3)
    c: Coincident(g3,g4)
    c: Coincident(g4,g5)
    c: Horizontal(g5)
    c: Coincident(g5,g6)
    c: Vertical(g6)
    c: Coincident(g6,g7)
    c: Coincident(g7,g0)
    c: Horizontal(g7)
    c: Coincident(g8,g6)
    c: PointOnObject(g8,g-3)
    c: Vertical(g8)
    c: Coincident(g9,g5)
    c: PointOnObject(g9,g-1)
    c: Vertical(g9)
    c: Coincident(g10,g5)
    c: PointOnObject(g10,g-4)
    c: Coincident(g11,g3)
    c: PointOnObject(g11,g-6)
    c: Horizontal(g11)
    c: Coincident(g12,g0)
    c: PointOnObject(g12,g-5)
    c: Horizontal(g12)
    c: Equal(g12,g11)
    c: Vertical(g4)
    c: Horizontal(g10)
    c: DistanceY(g8,g8) = 1.5
    c: DistanceY(g0,g0) = 1.8
    c: Equal(g0,g4)
    c: DistanceX(g11,g11) = 2
    c: DistanceX(g10,g10) = 3
    c: DistanceX(g6,g1) = 3
    c: Equal(g8,g9)
FEATURE [PartDesign::Pocket] Pocket014
  BaseFeature = -> Chamfer001
  Direction = (0,0,1)
  Length = 5
  Length2 = 5
  Placement = pos=(0,0,0) rot=(1,0,0;1.5708rad)
  Profile = -> Sketch024
  ReferenceAxis = -> Sketch024 [N_Axis]
  Refine = true
  Suppressed = false
  Type = 0
FEATURE [PartDesign::Body] Body001  label="top"
  Group = -> [Sketch001,Pad001,Sketch002,Pocket,DatumPlane,Sketch003,Pocket001,Sketch004,Pocket002,Sketch005,Pocket003,Fillet,Sketch006,Pocket004,Sketch007,Pocket005,Sketch008,Pad002,Sketch009,Pocket006,Pad008,Pad009,Sketch023,Pocket013,Chamfer001,Sketch024,Pocket014]
  Origin = -> Origin036
  Placement = pos=(0,-30.35,0) rot=(0,0,1;0rad)
  Tip = -> Pocket014
FEATURE [Sketcher::SketchObject] Sketch025
  AttachmentSupport = -> [Pocket009]
  FullyConstrained = true
  MapMode = 5
  sketch-geometry (8):
    g0: LineSegment StartX=25.34 StartY=-1.5 StartZ=0 EndX=25.34 EndY=-3.3 EndZ=0
    g1: LineSegment StartX=25.34 StartY=-3.3 StartZ=0 EndX=-26.96 EndY=-3.3 EndZ=0
    g2: LineSegment StartX=-26.96 StartY=-3.3 StartZ=0 EndX=-26.96 EndY=-29 EndZ=0
    g3: LineSegment StartX=-26.96 StartY=-29 StartZ=0 EndX=25.34 EndY=-29 EndZ=0
    g4: LineSegment StartX=25.34 StartY=-29 StartZ=0 EndX=25.34 EndY=-30.8 EndZ=0
    g5: LineSegment StartX=25.34 StartY=-30.8 StartZ=0 EndX=-29.96 EndY=-30.8 EndZ=0
    g6: LineSegment StartX=-29.96 StartY=-30.8 StartZ=0 EndX=-29.96 EndY=-1.5 EndZ=0
    g7: LineSegment StartX=-29.96 StartY=-1.5 StartZ=0 EndX=25.34 EndY=-1.5 EndZ=0
  constraints (24):
    c: Vertical(g0)
    c: Coincident(g0,g1)
    c: Horizontal(g1)
    c: Coincident(g1,g2)
    c: Vertical(g2)
    c: Coincident(g2,g3)
    c: Horizontal(g3)
    c: Coincident(g3,g4)
    c: Vertical(g4)
    c: Coincident(g4,g5)
    c: Horizontal(g5)
    c: Coincident(g5,g6)
    c: Vertical(g6)
    c: Coincident(g6,g7)
    c: Coincident(g7,g0)
    c: Horizontal(g7)
    c: DistanceX(g0) = 25.34
    c: DistanceY(g0) = -1.5
    c: DistanceX(g7,g7) = 55.3
    c: DistanceX(g1,g1) = 52.3
    c: DistanceY(g0,g0) = 1.8
    c: DistanceY(g2,g2) = 25.7
    c: Equal(g4,g0)
    c: Equal(g1,g3)
FEATURE [PartDesign::Pocket] Pocket015
  BaseFeature = -> Pocket009
  Direction = (0,0,-1)
  Length = 1.5
  Length2 = 5
  Profile = -> Sketch025
  ReferenceAxis = -> Sketch025 [N_Axis]
  Refine = true
  Suppressed = false
  Type = 0
FEATURE [PartDesign::Chamfer] Chamfer002
  Angle = 45
  Base = -> Pocket015 [Edge42,Edge50,Edge55,Edge52]
  BaseFeature = -> Pocket015
  ChamferType = 0
  FlipDirection = false
  Refine = true
  Size = 0.4
  Size2 = 1
  SupportTransform = false
  Suppressed = false
  UseAllEdges = false
FEATURE [PartDesign::Body] Body002  label="bottom"
  Group = -> [Sketch011,Pad003,Fillet001,Sketch012,Pad004,Sketch013,Sketch014,Pad005,Sketch015,Pocket008,Pocket009,Sketch025,Pocket015,Chamfer002]
  Origin = -> Origin037
  Placement = pos=(0,-30.35,0) rot=(0,0,1;0rad)
  Tip = -> Chamfer002
FEATURE [Sketcher::SketchObject] Sketch026
  AttachmentSupport = -> [XY_Plane040]
  FullyConstrained = true
  MapMode = 5
  sketch-geometry (13):
    g0: LineSegment StartX=24 StartY=-32.15 StartZ=0 EndX=24 EndY=-33.35 EndZ=0
    g1: LineSegment StartX=24 StartY=-33.35 StartZ=0 EndX=-27.26 EndY=-33.35 EndZ=0
    g2: LineSegment StartX=-27.26 StartY=-33.35 StartZ=0 EndX=-27.26 EndY=-59.65 EndZ=0
    g3: LineSegment StartX=-27.26 StartY=-59.65 StartZ=0 EndX=24 EndY=-59.65 EndZ=0
    g4: LineSegment StartX=24 StartY=-59.65 StartZ=0 EndX=24 EndY=-60.85 EndZ=0
    g5: LineSegment StartX=24 StartY=-60.85 StartZ=0 EndX=-29.66 EndY=-60.85 EndZ=0
    g6: LineSegment StartX=-29.66 StartY=-60.85 StartZ=0 EndX=-29.66 EndY=-32.15 EndZ=0
    g7: LineSegment StartX=-29.66 StartY=-32.15 StartZ=0 EndX=24 EndY=-32.15 EndZ=0
    g8: LineSegment StartX=-29.66 StartY=-32.15 StartZ=0 EndX=-29.66 EndY=-31.85 EndZ=0
    g9: LineSegment StartX=-29.66 StartY=-32.15 StartZ=0 EndX=-29.96 EndY=-32.15 EndZ=0
    g10: LineSegment StartX=24 StartY=-33.35 StartZ=0 EndX=24 EndY=-33.65 EndZ=0
    g11: LineSegment StartX=-27.26 StartY=-33.65 StartZ=0 EndX=-26.96 EndY=-33.65 EndZ=0
    g12: LineSegment StartX=-29.66 StartY=-60.85 StartZ=0 EndX=-29.66 EndY=-61.15 EndZ=0
  constraints (40):
    c: Coincident(g0,g1)
    c: Horizontal(g1)
    c: Coincident(g1,g2)
    c: Vertical(g2)
    c: Coincident(g2,g3)
    c: Horizontal(g3)
    c: Coincident(g3,g4)
    c: Coincident(g4,g5)
    c: Horizontal(g5)
    c: Coincident(g5,g6)
    c: Vertical(g6)
    c: Coincident(g6,g7)
    c: Coincident(g7,g0)
    c: Horizontal(g7)
    c: Coincident(g8,g6)
    c: Vertical(g8)
    c: Coincident(g9,g6)
    c: Horizontal(g9)
    c: DistanceX(g9,g9) = 0.3
    c: DistanceX(g9) = -29.96
    c: Equal(g8,g9)
    c: DistanceY(g8) = -31.85
    c: Vertical(g0)
    c: DistanceX(g7,g7) = 53.66
    c: Coincident(g10,g0)
    c: Vertical(g10)
    c: Equal(g9,g10)
    c: DistanceY(g10) = -33.65
    c: PointOnObject(g11,g2)
    c: Horizontal(g11)
    c: PointOnObject(g10,g11)
    c: Equal(g9,g11)
    c: DistanceX(g11) = -26.96
    c: Coincident(g12,g5)
    c: Vertical(g12)
    c: Equal(g12,g9)
    c: DistanceY(g12) = -61.15
    c: Equal(g7,g5)
    c: Vertical(g4)
    c: Equal(g4,g0)
FEATURE [PartDesign::Pad] Pad015
  Direction = (0,0,1)
  Length = 5
  Length2 = 10
  Profile = -> Sketch026
  ReferenceAxis = -> Sketch026 [N_Axis]
  Refine = true
  Suppressed = false
  Type = 0
FEATURE [PartDesign::Body] Body005  label="junta"
  Group = -> [Sketch026,Pad015]
  Origin = -> Origin040
  Placement = pos=(0,0,-0.9) rot=(0,0,1;0rad)
  Tip = -> Pad015
